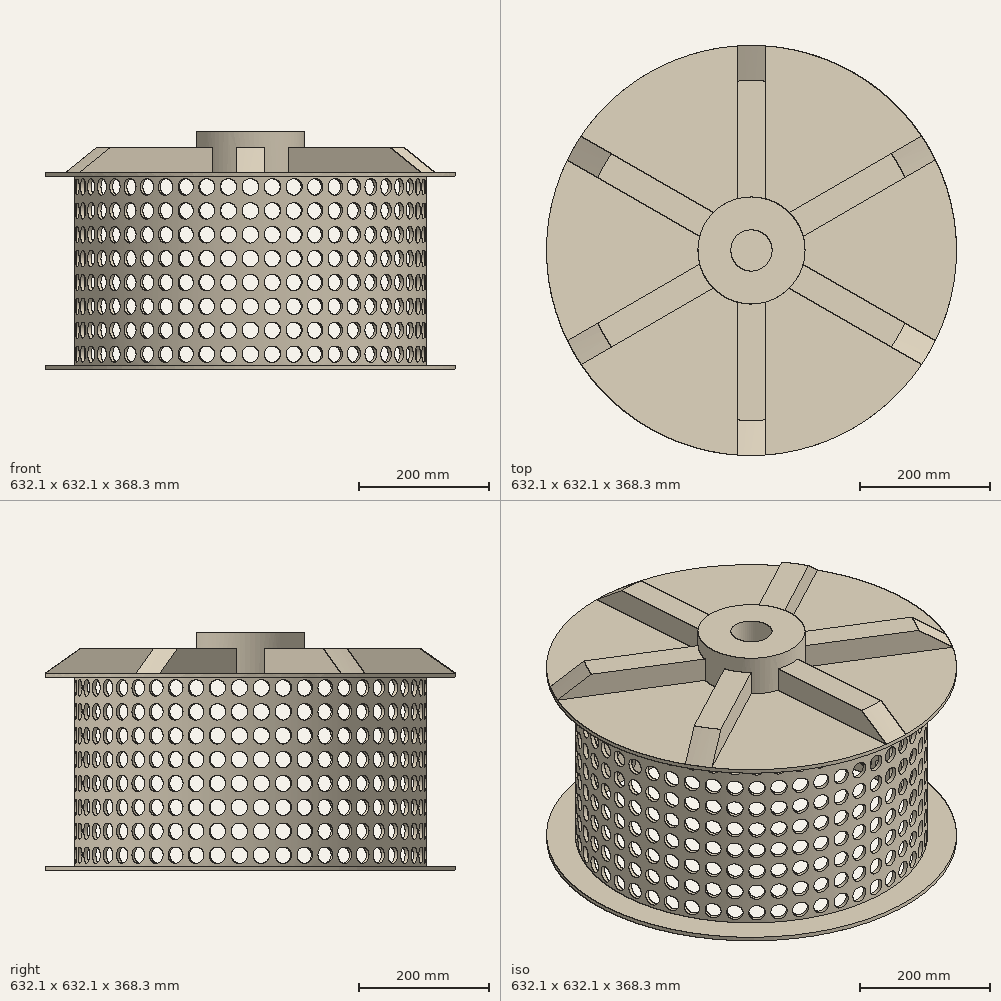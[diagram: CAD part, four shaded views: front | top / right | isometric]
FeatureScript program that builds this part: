
annotation { "Feature Type Name" : "Feature", "Feature Type Description" : "" }
export const myFeature = defineFeature(function(context is Context, id is Id, definition is map)
    precondition{}
    {
        {
            var Q0;
            Q0=qCreatedBy(makeId("Front.planeOp"),FACE);
            var sketch = newSketch(context, id + "F0", { "sketchPlane" : qUnion([Q0])});
            skLineSegment(sketch, "E0", {"start": v(265.27, 0) * mm, "end": v(316.07, 0) * mm});
            skLineSegment(sketch, "E1", {"start": v(316.07, 0) * mm, "end": v(316.07, 6.35) * mm});
            skLineSegment(sketch, "E2", {"start": v(316.07, 6.35) * mm, "end": v(265.27, 6.35) * mm});
            skLineSegment(sketch, "E3", {"start": v(265.27, 6.35) * mm, "end": v(265.27, 0) * mm});
            skLineSegment(sketch, "E4", {"start": v(265.27, 6.35) * mm, "end": v(265.27, 298.45) * mm});
            skLineSegment(sketch, "E5", {"start": v(265.27, 298.45) * mm, "end": v(271.62, 298.45) * mm});
            skLineSegment(sketch, "E6", {"start": v(271.62, 298.45) * mm, "end": v(271.62, 6.35) * mm});
            skLineSegment(sketch, "E7", {"start": v(265.27, 298.45) * mm, "end": v(265.27, 304.8) * mm});
            skLineSegment(sketch, "E8", {"start": v(265.27, 304.8) * mm, "end": v(316.07, 304.8) * mm});
            skLineSegment(sketch, "E9", {"start": v(316.07, 304.8) * mm, "end": v(316.07, 298.45) * mm});
            skLineSegment(sketch, "E10", {"start": v(316.07, 298.45) * mm, "end": v(271.62, 298.45) * mm});
            skLineSegment(sketch, "E11", {"start": v(0, -69.14) * mm, "end": v(0, 356.1) * mm, "construction": true});
            skLineSegment(sketch, "E12", {"start": v(265.27, 304.8) * mm, "end": v(0, 304.8) * mm});
            skLineSegment(sketch, "E13", {"start": v(0, 304.8) * mm, "end": v(0, 298.45) * mm});
            skLineSegment(sketch, "E14", {"start": v(0, 298.45) * mm, "end": v(265.27, 298.45) * mm});
            skSolve(sketch);
        }
        {
            var Q0;
            Q0=qSketchRegion(id+"F0",true);
            var Q1;
            Q1=sQuery(id+"F0.wireOp",EDGE,"E11");
            revolve(context, id + "F1", {"entities" : qUnion([Q0]), "axis" : qUnion([Q1]), "revolveType" : RevolveType.FULL});
        }
        {
            var Q0;
            Q0=makeQuery(id+"F1.opRevolve","SWEPT_FACE",FACE,{"disambiguationData":[OSD([sQuery(id+"F0.wireOp",EDGE,"E8"),sQuery(id+"F0.wireOp",EDGE,"E12")])]});
            var sketch = newSketch(context, id + "F2", { "sketchPlane" : qUnion([Q0])});
            skCircle(sketch, "E15", {"center": v(0, 0) * mm, "radius": 31.75 * mm});
            skCircle(sketch, "E16", {"center": v(0, 0) * mm, "radius": 82.55 * mm});
            skLineSegment(sketch, "E17.bottom", {"start": v(21.06, 315.86) * mm, "end": v(-21.41, 315.96) * mm});
            skLineSegment(sketch, "E17.left", {"start": v(21.06, 315.86) * mm, "end": v(21.41, 79.72) * mm});
            skLineSegment(sketch, "E17.right", {"start": v(-21.41, 315.96) * mm, "end": v(-21.06, 79.82) * mm});
            skPoint(sketch, "E17.middle", {"position": v(0, 197.84) * mm});
            skPoint(sketch, "E18.center", {"position": v(-0.43, 1.69) * mm});
            skLineSegment(sketch, "E19.1.0", {"start": v(-263.02, 176.17) * mm, "end": v(-284.33, 139.44) * mm});
            skLineSegment(sketch, "E19.1.1", {"start": v(-263.02, 176.17) * mm, "end": v(-58.34, 58.4) * mm});
            skLineSegment(sketch, "E19.1.2", {"start": v(-284.33, 139.44) * mm, "end": v(-79.65, 21.67) * mm});
            skLineSegment(sketch, "E19.2.0", {"start": v(-284.08, -139.7) * mm, "end": v(-262.92, -176.52) * mm});
            skLineSegment(sketch, "E19.2.1", {"start": v(-284.08, -139.7) * mm, "end": v(-79.75, -21.32) * mm});
            skLineSegment(sketch, "E19.2.2", {"start": v(-262.92, -176.52) * mm, "end": v(-58.6, -58.15) * mm});
            skLineSegment(sketch, "E19.3.0", {"start": v(-21.06, -315.86) * mm, "end": v(21.41, -315.96) * mm});
            skLineSegment(sketch, "E19.3.1", {"start": v(-21.06, -315.86) * mm, "end": v(-21.41, -79.72) * mm});
            skLineSegment(sketch, "E19.3.2", {"start": v(21.41, -315.96) * mm, "end": v(21.06, -79.82) * mm});
            skLineSegment(sketch, "E19.4.0", {"start": v(263.02, -176.17) * mm, "end": v(284.33, -139.44) * mm});
            skLineSegment(sketch, "E19.4.1", {"start": v(263.02, -176.17) * mm, "end": v(58.34, -58.4) * mm});
            skLineSegment(sketch, "E19.4.2", {"start": v(284.33, -139.44) * mm, "end": v(79.65, -21.67) * mm});
            skLineSegment(sketch, "E19.5.0", {"start": v(284.08, 139.7) * mm, "end": v(262.92, 176.52) * mm});
            skLineSegment(sketch, "E19.5.1", {"start": v(284.08, 139.7) * mm, "end": v(79.75, 21.32) * mm});
            skLineSegment(sketch, "E19.5.2", {"start": v(262.92, 176.52) * mm, "end": v(58.6, 58.15) * mm});
            skSolve(sketch);
        }
        {
            var Q0;
            Q0=makeQuery(id+"F2.imprint","IMPRINT",FACE,{"disambiguationData":[TD([[makeQuery(id+"F2.imprint","IMPRINT",EDGE,{"derivedFrom":sQuery(id+"F2.wireOp",EDGE,"E15")}),-1.0]])]});
            extrude(context, id + "F3", {"entities" : qUnion([Q0]), "operationType" : NewBodyOperationType.ADD, "depth" : 63.5 * mm, "offsetDistance" : 25.4 * mm});
        }
        {
            var Q0;
            {var subQ0=sQuery(id+"F2.wireOp",EDGE,"E19.1.1");var subQ1=sQuery(id+"F2.wireOp",EDGE,"E16");var subQ2=makeQuery(id+"F2.imprint","INTERSECT",VERTEX,{"derivedFrom":[subQ1,subQ0]});Q0=makeQuery(id+"F2.imprint","IMPRINT",FACE,{"disambiguationData":[TD([[makeQuery(id+"F2.imprint","IMPRINT",EDGE,{"disambiguationData":[TD([[subQ2,-1.0]])],"derivedFrom":subQ1}),-1.0]])]});}
            var Q1;
            {var subQ0=sQuery(id+"F2.wireOp",EDGE,"E17.left");var subQ1=sQuery(id+"F2.wireOp",EDGE,"E16");var subQ2=makeQuery(id+"F2.imprint","INTERSECT",VERTEX,{"derivedFrom":[subQ1,subQ0]});Q1=makeQuery(id+"F2.imprint","IMPRINT",FACE,{"disambiguationData":[TD([[makeQuery(id+"F2.imprint","IMPRINT",EDGE,{"disambiguationData":[TD([[subQ2,-1.0]])],"derivedFrom":subQ1}),-1.0]])]});}
            var Q2;
            {var subQ0=sQuery(id+"F2.wireOp",EDGE,"E19.5.1");var subQ1=sQuery(id+"F2.wireOp",EDGE,"E16");var subQ2=makeQuery(id+"F2.imprint","INTERSECT",VERTEX,{"derivedFrom":[subQ1,subQ0]});Q2=makeQuery(id+"F2.imprint","IMPRINT",FACE,{"disambiguationData":[TD([[makeQuery(id+"F2.imprint","IMPRINT",EDGE,{"disambiguationData":[TD([[subQ2,-1.0]])],"derivedFrom":subQ1}),-1.0]])]});}
            var Q3;
            {var subQ0=sQuery(id+"F2.wireOp",EDGE,"E19.4.1");var subQ1=sQuery(id+"F2.wireOp",EDGE,"E16");var subQ2=makeQuery(id+"F2.imprint","INTERSECT",VERTEX,{"derivedFrom":[subQ1,subQ0]});Q3=makeQuery(id+"F2.imprint","IMPRINT",FACE,{"disambiguationData":[TD([[makeQuery(id+"F2.imprint","IMPRINT",EDGE,{"disambiguationData":[TD([[subQ2,-1.0]])],"derivedFrom":subQ1}),-1.0]])]});}
            var Q4;
            {var subQ0=sQuery(id+"F2.wireOp",EDGE,"E19.3.1");var subQ1=sQuery(id+"F2.wireOp",EDGE,"E16");var subQ2=makeQuery(id+"F2.imprint","INTERSECT",VERTEX,{"derivedFrom":[subQ1,subQ0]});Q4=makeQuery(id+"F2.imprint","IMPRINT",FACE,{"disambiguationData":[TD([[makeQuery(id+"F2.imprint","IMPRINT",EDGE,{"disambiguationData":[TD([[subQ2,-1.0]])],"derivedFrom":subQ1}),-1.0]])]});}
            var Q5;
            {var subQ0=sQuery(id+"F2.wireOp",EDGE,"E19.2.1");var subQ1=sQuery(id+"F2.wireOp",EDGE,"E16");var subQ2=makeQuery(id+"F2.imprint","INTERSECT",VERTEX,{"derivedFrom":[subQ1,subQ0]});Q5=makeQuery(id+"F2.imprint","IMPRINT",FACE,{"disambiguationData":[TD([[makeQuery(id+"F2.imprint","IMPRINT",EDGE,{"disambiguationData":[TD([[subQ2,-1.0]])],"derivedFrom":subQ1}),-1.0]])]});}
            extrude(context, id + "F4", {"entities" : qUnion([Q0, Q1, Q2, Q3, Q4, Q5]), "operationType" : NewBodyOperationType.ADD, "depth" : 38.1 * mm, "offsetDistance" : 25.4 * mm});
        }
        {
            var Q0;
            Q0=qCreatedBy(makeId("Front.planeOp"),FACE);
            var sketch = newSketch(context, id + "F5", { "sketchPlane" : qUnion([Q0])});
            skPoint(sketch, "E20.0", {"position": v(316.07, 304.8) * mm});
            skLineSegment(sketch, "E21", {"start": v(316.07, 304.8) * mm, "end": v(257.94, 345.81) * mm});
            skLineSegment(sketch, "E22", {"start": v(257.94, 345.81) * mm, "end": v(316.07, 345.81) * mm});
            skLineSegment(sketch, "E23", {"start": v(316.07, 345.81) * mm, "end": v(316.07, 304.8) * mm});
            skSolve(sketch);
        }
        {
            var Q0;
            Q0=makeQuery(id+"F5.imprint","IMPRINT",FACE,{"disambiguationData":[TD([[makeQuery(id+"F5.imprint","IMPRINT",EDGE,{"derivedFrom":sQuery(id+"F5.wireOp",EDGE,"E21")}),-1.0]])]});
            var Q1;
            Q1=makeQuery(id+"F3.opExtrude","CAP_EDGE",EDGE,{"disambiguationData":[OSD([sQuery(id+"F2.wireOp",EDGE,"E16")])],"isStart":false});
            revolve(context, id + "F6", {"operationType" : NewBodyOperationType.REMOVE, "entities" : qUnion([Q0]), "axis" : qUnion([Q1]), "revolveType" : RevolveType.FULL, "oppositeDirection" : true});
        }
        {
            var Q0;
            Q0=qCreatedBy(makeId("Front.planeOp"),FACE);
            cPlane(context, id + "F7", {"entities" : qUnion([Q0]), "cplaneType" : CPlaneType.OFFSET, "offset" : 326.14 * mm, "width" : 152.4 * mm, "height" : 152.4 * mm});
        }
        {
            var Q0;
            Q0=qCreatedBy(id+"F7.planeOp",FACE);
            var sketch = newSketch(context, id + "F8", { "sketchPlane" : qUnion([Q0])});
            skCircle(sketch, "E24", {"center": v(0, 24.22) * mm, "radius": 12.7 * mm});
            skCircle(sketch, "E25.0.1.0", {"center": v(0, 61.05) * mm, "radius": 12.7 * mm});
            skCircle(sketch, "E25.0.2.0", {"center": v(0, 97.88) * mm, "radius": 12.7 * mm});
            skCircle(sketch, "E25.0.3.0", {"center": v(0, 134.7) * mm, "radius": 12.7 * mm});
            skCircle(sketch, "E25.0.4.0", {"center": v(0, 171.54) * mm, "radius": 12.7 * mm});
            skCircle(sketch, "E25.0.5.0", {"center": v(0, 208.37) * mm, "radius": 12.7 * mm});
            skCircle(sketch, "E25.0.6.0", {"center": v(0, 245.2) * mm, "radius": 12.7 * mm});
            skCircle(sketch, "E25.0.7.0", {"center": v(0, 282.03) * mm, "radius": 12.7 * mm});
            skLineSegment(sketch, "E25.direction1", {"start": v(0, 24.22) * mm, "end": v(25.4, 24.22) * mm, "construction": true});
            skLineSegment(sketch, "E25.direction2", {"start": v(0, 24.22) * mm, "end": v(0, 61.05) * mm, "construction": true});
            skSolve(sketch);
        }
        {
            var Q0;
            Q0=qSketchRegion(id+"F8",true);
            extrude(context, id + "F9", {"entities" : qUnion([Q0]), "oppositeDirection" : true, "depth" : 161.54 * mm, "offsetDistance" : 25.4 * mm});
        }
        {
            var Q0;
            Q0=makeQuery(id+"F9.opExtrude","SWEPT_BODY",BODY,{"disambiguationData":[OSD([sQuery(id+"F8.wireOp",EDGE,"E25.0.7.0")])]});
            var Q1;
            Q1=makeQuery(id+"F9.opExtrude","SWEPT_BODY",BODY,{"disambiguationData":[OSD([sQuery(id+"F8.wireOp",EDGE,"E25.0.6.0")])]});
            var Q2;
            Q2=makeQuery(id+"F9.opExtrude","SWEPT_BODY",BODY,{"disambiguationData":[OSD([sQuery(id+"F8.wireOp",EDGE,"E25.0.5.0")])]});
            var Q3;
            Q3=makeQuery(id+"F9.opExtrude","SWEPT_BODY",BODY,{"disambiguationData":[OSD([sQuery(id+"F8.wireOp",EDGE,"E25.0.4.0")])]});
            var Q4;
            Q4=makeQuery(id+"F9.opExtrude","SWEPT_BODY",BODY,{"disambiguationData":[OSD([sQuery(id+"F8.wireOp",EDGE,"E25.0.3.0")])]});
            var Q5;
            Q5=makeQuery(id+"F9.opExtrude","SWEPT_BODY",BODY,{"disambiguationData":[OSD([sQuery(id+"F8.wireOp",EDGE,"E25.0.2.0")])]});
            var Q6;
            Q6=makeQuery(id+"F9.opExtrude","SWEPT_BODY",BODY,{"disambiguationData":[OSD([sQuery(id+"F8.wireOp",EDGE,"E25.0.1.0")])]});
            var Q7;
            Q7=makeQuery(id+"F9.opExtrude","SWEPT_BODY",BODY,{"disambiguationData":[OSD([sQuery(id+"F8.wireOp",EDGE,"E24")])]});
            var Q8;
            Q8=makeQuery(id+"F3.opExtrude","CAP_EDGE",EDGE,{"disambiguationData":[OSD([sQuery(id+"F2.wireOp",EDGE,"E16")])],"isStart":false});
            circularPattern(context, id + "F10", {"entities" : qUnion([Q0, Q1, Q2, Q3, Q4, Q5, Q6, Q7]), "axis" : qUnion([Q8]), "angle" : 360 * degree, "instanceCount" : 50, "equalSpace" : true});
        }
        {
            var Q0;
            Q0=makeQuery(id+"F9.opExtrude","SWEPT_BODY",BODY,{"disambiguationData":[OSD([sQuery(id+"F8.wireOp",EDGE,"E24")])]});
            var Q1;
            Q1=makeQuery(id+"F9.opExtrude","SWEPT_BODY",BODY,{"disambiguationData":[OSD([sQuery(id+"F8.wireOp",EDGE,"E25.0.1.0")])]});
            var Q2;
            Q2=makeQuery(id+"F9.opExtrude","SWEPT_BODY",BODY,{"disambiguationData":[OSD([sQuery(id+"F8.wireOp",EDGE,"E25.0.2.0")])]});
            var Q3;
            Q3=makeQuery(id+"F9.opExtrude","SWEPT_BODY",BODY,{"disambiguationData":[OSD([sQuery(id+"F8.wireOp",EDGE,"E25.0.3.0")])]});
            var Q4;
            Q4=makeQuery(id+"F9.opExtrude","SWEPT_BODY",BODY,{"disambiguationData":[OSD([sQuery(id+"F8.wireOp",EDGE,"E25.0.4.0")])]});
            var Q5;
            Q5=makeQuery(id+"F9.opExtrude","SWEPT_BODY",BODY,{"disambiguationData":[OSD([sQuery(id+"F8.wireOp",EDGE,"E25.0.5.0")])]});
            var Q6;
            Q6=makeQuery(id+"F9.opExtrude","SWEPT_BODY",BODY,{"disambiguationData":[OSD([sQuery(id+"F8.wireOp",EDGE,"E25.0.6.0")])]});
            var Q7;
            Q7=makeQuery(id+"F9.opExtrude","SWEPT_BODY",BODY,{"disambiguationData":[OSD([sQuery(id+"F8.wireOp",EDGE,"E25.0.7.0")])]});
            var Q8;
            Q8=makeQuery(id+"F10.opPattern","COPY",BODY,{"derivedFrom":makeQuery(id+"F9.opExtrude","SWEPT_BODY",BODY,{"disambiguationData":[OSD([sQuery(id+"F8.wireOp",EDGE,"E24")])]}),"instanceName":"1"});
            var Q9;
            Q9=makeQuery(id+"F10.opPattern","COPY",BODY,{"derivedFrom":makeQuery(id+"F9.opExtrude","SWEPT_BODY",BODY,{"disambiguationData":[OSD([sQuery(id+"F8.wireOp",EDGE,"E25.0.1.0")])]}),"instanceName":"1"});
            var Q10;
            Q10=makeQuery(id+"F10.opPattern","COPY",BODY,{"derivedFrom":makeQuery(id+"F9.opExtrude","SWEPT_BODY",BODY,{"disambiguationData":[OSD([sQuery(id+"F8.wireOp",EDGE,"E25.0.2.0")])]}),"instanceName":"1"});
            var Q11;
            Q11=makeQuery(id+"F10.opPattern","COPY",BODY,{"derivedFrom":makeQuery(id+"F9.opExtrude","SWEPT_BODY",BODY,{"disambiguationData":[OSD([sQuery(id+"F8.wireOp",EDGE,"E25.0.3.0")])]}),"instanceName":"1"});
            var Q12;
            Q12=makeQuery(id+"F10.opPattern","COPY",BODY,{"derivedFrom":makeQuery(id+"F9.opExtrude","SWEPT_BODY",BODY,{"disambiguationData":[OSD([sQuery(id+"F8.wireOp",EDGE,"E25.0.4.0")])]}),"instanceName":"1"});
            var Q13;
            Q13=makeQuery(id+"F10.opPattern","COPY",BODY,{"derivedFrom":makeQuery(id+"F9.opExtrude","SWEPT_BODY",BODY,{"disambiguationData":[OSD([sQuery(id+"F8.wireOp",EDGE,"E25.0.5.0")])]}),"instanceName":"1"});
            var Q14;
            Q14=makeQuery(id+"F10.opPattern","COPY",BODY,{"derivedFrom":makeQuery(id+"F9.opExtrude","SWEPT_BODY",BODY,{"disambiguationData":[OSD([sQuery(id+"F8.wireOp",EDGE,"E25.0.6.0")])]}),"instanceName":"1"});
            var Q15;
            Q15=makeQuery(id+"F10.opPattern","COPY",BODY,{"derivedFrom":makeQuery(id+"F9.opExtrude","SWEPT_BODY",BODY,{"disambiguationData":[OSD([sQuery(id+"F8.wireOp",EDGE,"E25.0.7.0")])]}),"instanceName":"1"});
            var Q16;
            Q16=makeQuery(id+"F10.opPattern","COPY",BODY,{"derivedFrom":makeQuery(id+"F9.opExtrude","SWEPT_BODY",BODY,{"disambiguationData":[OSD([sQuery(id+"F8.wireOp",EDGE,"E24")])]}),"instanceName":"2"});
            var Q17;
            Q17=makeQuery(id+"F10.opPattern","COPY",BODY,{"derivedFrom":makeQuery(id+"F9.opExtrude","SWEPT_BODY",BODY,{"disambiguationData":[OSD([sQuery(id+"F8.wireOp",EDGE,"E25.0.1.0")])]}),"instanceName":"2"});
            var Q18;
            Q18=makeQuery(id+"F10.opPattern","COPY",BODY,{"derivedFrom":makeQuery(id+"F9.opExtrude","SWEPT_BODY",BODY,{"disambiguationData":[OSD([sQuery(id+"F8.wireOp",EDGE,"E25.0.2.0")])]}),"instanceName":"2"});
            var Q19;
            Q19=makeQuery(id+"F10.opPattern","COPY",BODY,{"derivedFrom":makeQuery(id+"F9.opExtrude","SWEPT_BODY",BODY,{"disambiguationData":[OSD([sQuery(id+"F8.wireOp",EDGE,"E25.0.3.0")])]}),"instanceName":"2"});
            var Q20;
            Q20=makeQuery(id+"F10.opPattern","COPY",BODY,{"derivedFrom":makeQuery(id+"F9.opExtrude","SWEPT_BODY",BODY,{"disambiguationData":[OSD([sQuery(id+"F8.wireOp",EDGE,"E25.0.4.0")])]}),"instanceName":"2"});
            var Q21;
            Q21=makeQuery(id+"F10.opPattern","COPY",BODY,{"derivedFrom":makeQuery(id+"F9.opExtrude","SWEPT_BODY",BODY,{"disambiguationData":[OSD([sQuery(id+"F8.wireOp",EDGE,"E25.0.5.0")])]}),"instanceName":"2"});
            var Q22;
            Q22=makeQuery(id+"F10.opPattern","COPY",BODY,{"derivedFrom":makeQuery(id+"F9.opExtrude","SWEPT_BODY",BODY,{"disambiguationData":[OSD([sQuery(id+"F8.wireOp",EDGE,"E25.0.6.0")])]}),"instanceName":"2"});
            var Q23;
            Q23=makeQuery(id+"F10.opPattern","COPY",BODY,{"derivedFrom":makeQuery(id+"F9.opExtrude","SWEPT_BODY",BODY,{"disambiguationData":[OSD([sQuery(id+"F8.wireOp",EDGE,"E25.0.7.0")])]}),"instanceName":"2"});
            var Q24;
            Q24=makeQuery(id+"F10.opPattern","COPY",BODY,{"derivedFrom":makeQuery(id+"F9.opExtrude","SWEPT_BODY",BODY,{"disambiguationData":[OSD([sQuery(id+"F8.wireOp",EDGE,"E24")])]}),"instanceName":"3"});
            var Q25;
            Q25=makeQuery(id+"F10.opPattern","COPY",BODY,{"derivedFrom":makeQuery(id+"F9.opExtrude","SWEPT_BODY",BODY,{"disambiguationData":[OSD([sQuery(id+"F8.wireOp",EDGE,"E25.0.1.0")])]}),"instanceName":"3"});
            var Q26;
            Q26=makeQuery(id+"F10.opPattern","COPY",BODY,{"derivedFrom":makeQuery(id+"F9.opExtrude","SWEPT_BODY",BODY,{"disambiguationData":[OSD([sQuery(id+"F8.wireOp",EDGE,"E25.0.2.0")])]}),"instanceName":"3"});
            var Q27;
            Q27=makeQuery(id+"F10.opPattern","COPY",BODY,{"derivedFrom":makeQuery(id+"F9.opExtrude","SWEPT_BODY",BODY,{"disambiguationData":[OSD([sQuery(id+"F8.wireOp",EDGE,"E25.0.3.0")])]}),"instanceName":"3"});
            var Q28;
            Q28=makeQuery(id+"F10.opPattern","COPY",BODY,{"derivedFrom":makeQuery(id+"F9.opExtrude","SWEPT_BODY",BODY,{"disambiguationData":[OSD([sQuery(id+"F8.wireOp",EDGE,"E25.0.4.0")])]}),"instanceName":"3"});
            var Q29;
            Q29=makeQuery(id+"F10.opPattern","COPY",BODY,{"derivedFrom":makeQuery(id+"F9.opExtrude","SWEPT_BODY",BODY,{"disambiguationData":[OSD([sQuery(id+"F8.wireOp",EDGE,"E25.0.5.0")])]}),"instanceName":"3"});
            var Q30;
            Q30=makeQuery(id+"F10.opPattern","COPY",BODY,{"derivedFrom":makeQuery(id+"F9.opExtrude","SWEPT_BODY",BODY,{"disambiguationData":[OSD([sQuery(id+"F8.wireOp",EDGE,"E25.0.6.0")])]}),"instanceName":"3"});
            var Q31;
            Q31=makeQuery(id+"F10.opPattern","COPY",BODY,{"derivedFrom":makeQuery(id+"F9.opExtrude","SWEPT_BODY",BODY,{"disambiguationData":[OSD([sQuery(id+"F8.wireOp",EDGE,"E25.0.7.0")])]}),"instanceName":"3"});
            var Q32;
            Q32=makeQuery(id+"F10.opPattern","COPY",BODY,{"derivedFrom":makeQuery(id+"F9.opExtrude","SWEPT_BODY",BODY,{"disambiguationData":[OSD([sQuery(id+"F8.wireOp",EDGE,"E24")])]}),"instanceName":"4"});
            var Q33;
            Q33=makeQuery(id+"F10.opPattern","COPY",BODY,{"derivedFrom":makeQuery(id+"F9.opExtrude","SWEPT_BODY",BODY,{"disambiguationData":[OSD([sQuery(id+"F8.wireOp",EDGE,"E25.0.1.0")])]}),"instanceName":"4"});
            var Q34;
            Q34=makeQuery(id+"F10.opPattern","COPY",BODY,{"derivedFrom":makeQuery(id+"F9.opExtrude","SWEPT_BODY",BODY,{"disambiguationData":[OSD([sQuery(id+"F8.wireOp",EDGE,"E25.0.2.0")])]}),"instanceName":"4"});
            var Q35;
            Q35=makeQuery(id+"F10.opPattern","COPY",BODY,{"derivedFrom":makeQuery(id+"F9.opExtrude","SWEPT_BODY",BODY,{"disambiguationData":[OSD([sQuery(id+"F8.wireOp",EDGE,"E25.0.3.0")])]}),"instanceName":"4"});
            var Q36;
            Q36=makeQuery(id+"F10.opPattern","COPY",BODY,{"derivedFrom":makeQuery(id+"F9.opExtrude","SWEPT_BODY",BODY,{"disambiguationData":[OSD([sQuery(id+"F8.wireOp",EDGE,"E25.0.4.0")])]}),"instanceName":"4"});
            var Q37;
            Q37=makeQuery(id+"F10.opPattern","COPY",BODY,{"derivedFrom":makeQuery(id+"F9.opExtrude","SWEPT_BODY",BODY,{"disambiguationData":[OSD([sQuery(id+"F8.wireOp",EDGE,"E25.0.5.0")])]}),"instanceName":"4"});
            var Q38;
            Q38=makeQuery(id+"F10.opPattern","COPY",BODY,{"derivedFrom":makeQuery(id+"F9.opExtrude","SWEPT_BODY",BODY,{"disambiguationData":[OSD([sQuery(id+"F8.wireOp",EDGE,"E25.0.6.0")])]}),"instanceName":"4"});
            var Q39;
            Q39=makeQuery(id+"F10.opPattern","COPY",BODY,{"derivedFrom":makeQuery(id+"F9.opExtrude","SWEPT_BODY",BODY,{"disambiguationData":[OSD([sQuery(id+"F8.wireOp",EDGE,"E25.0.7.0")])]}),"instanceName":"4"});
            var Q40;
            Q40=makeQuery(id+"F10.opPattern","COPY",BODY,{"derivedFrom":makeQuery(id+"F9.opExtrude","SWEPT_BODY",BODY,{"disambiguationData":[OSD([sQuery(id+"F8.wireOp",EDGE,"E24")])]}),"instanceName":"5"});
            var Q41;
            Q41=makeQuery(id+"F10.opPattern","COPY",BODY,{"derivedFrom":makeQuery(id+"F9.opExtrude","SWEPT_BODY",BODY,{"disambiguationData":[OSD([sQuery(id+"F8.wireOp",EDGE,"E25.0.1.0")])]}),"instanceName":"5"});
            var Q42;
            Q42=makeQuery(id+"F10.opPattern","COPY",BODY,{"derivedFrom":makeQuery(id+"F9.opExtrude","SWEPT_BODY",BODY,{"disambiguationData":[OSD([sQuery(id+"F8.wireOp",EDGE,"E25.0.2.0")])]}),"instanceName":"5"});
            var Q43;
            Q43=makeQuery(id+"F10.opPattern","COPY",BODY,{"derivedFrom":makeQuery(id+"F9.opExtrude","SWEPT_BODY",BODY,{"disambiguationData":[OSD([sQuery(id+"F8.wireOp",EDGE,"E25.0.3.0")])]}),"instanceName":"5"});
            var Q44;
            Q44=makeQuery(id+"F10.opPattern","COPY",BODY,{"derivedFrom":makeQuery(id+"F9.opExtrude","SWEPT_BODY",BODY,{"disambiguationData":[OSD([sQuery(id+"F8.wireOp",EDGE,"E25.0.4.0")])]}),"instanceName":"5"});
            var Q45;
            Q45=makeQuery(id+"F10.opPattern","COPY",BODY,{"derivedFrom":makeQuery(id+"F9.opExtrude","SWEPT_BODY",BODY,{"disambiguationData":[OSD([sQuery(id+"F8.wireOp",EDGE,"E25.0.5.0")])]}),"instanceName":"5"});
            var Q46;
            Q46=makeQuery(id+"F10.opPattern","COPY",BODY,{"derivedFrom":makeQuery(id+"F9.opExtrude","SWEPT_BODY",BODY,{"disambiguationData":[OSD([sQuery(id+"F8.wireOp",EDGE,"E25.0.6.0")])]}),"instanceName":"5"});
            var Q47;
            Q47=makeQuery(id+"F10.opPattern","COPY",BODY,{"derivedFrom":makeQuery(id+"F9.opExtrude","SWEPT_BODY",BODY,{"disambiguationData":[OSD([sQuery(id+"F8.wireOp",EDGE,"E25.0.7.0")])]}),"instanceName":"5"});
            var Q48;
            Q48=makeQuery(id+"F10.opPattern","COPY",BODY,{"derivedFrom":makeQuery(id+"F9.opExtrude","SWEPT_BODY",BODY,{"disambiguationData":[OSD([sQuery(id+"F8.wireOp",EDGE,"E24")])]}),"instanceName":"6"});
            var Q49;
            Q49=makeQuery(id+"F10.opPattern","COPY",BODY,{"derivedFrom":makeQuery(id+"F9.opExtrude","SWEPT_BODY",BODY,{"disambiguationData":[OSD([sQuery(id+"F8.wireOp",EDGE,"E25.0.1.0")])]}),"instanceName":"6"});
            var Q50;
            Q50=makeQuery(id+"F10.opPattern","COPY",BODY,{"derivedFrom":makeQuery(id+"F9.opExtrude","SWEPT_BODY",BODY,{"disambiguationData":[OSD([sQuery(id+"F8.wireOp",EDGE,"E25.0.2.0")])]}),"instanceName":"6"});
            var Q51;
            Q51=makeQuery(id+"F10.opPattern","COPY",BODY,{"derivedFrom":makeQuery(id+"F9.opExtrude","SWEPT_BODY",BODY,{"disambiguationData":[OSD([sQuery(id+"F8.wireOp",EDGE,"E25.0.3.0")])]}),"instanceName":"6"});
            var Q52;
            Q52=makeQuery(id+"F10.opPattern","COPY",BODY,{"derivedFrom":makeQuery(id+"F9.opExtrude","SWEPT_BODY",BODY,{"disambiguationData":[OSD([sQuery(id+"F8.wireOp",EDGE,"E25.0.4.0")])]}),"instanceName":"6"});
            var Q53;
            Q53=makeQuery(id+"F10.opPattern","COPY",BODY,{"derivedFrom":makeQuery(id+"F9.opExtrude","SWEPT_BODY",BODY,{"disambiguationData":[OSD([sQuery(id+"F8.wireOp",EDGE,"E25.0.5.0")])]}),"instanceName":"6"});
            var Q54;
            Q54=makeQuery(id+"F10.opPattern","COPY",BODY,{"derivedFrom":makeQuery(id+"F9.opExtrude","SWEPT_BODY",BODY,{"disambiguationData":[OSD([sQuery(id+"F8.wireOp",EDGE,"E25.0.6.0")])]}),"instanceName":"6"});
            var Q55;
            Q55=makeQuery(id+"F10.opPattern","COPY",BODY,{"derivedFrom":makeQuery(id+"F9.opExtrude","SWEPT_BODY",BODY,{"disambiguationData":[OSD([sQuery(id+"F8.wireOp",EDGE,"E25.0.7.0")])]}),"instanceName":"6"});
            var Q56;
            Q56=makeQuery(id+"F10.opPattern","COPY",BODY,{"derivedFrom":makeQuery(id+"F9.opExtrude","SWEPT_BODY",BODY,{"disambiguationData":[OSD([sQuery(id+"F8.wireOp",EDGE,"E24")])]}),"instanceName":"7"});
            var Q57;
            Q57=makeQuery(id+"F10.opPattern","COPY",BODY,{"derivedFrom":makeQuery(id+"F9.opExtrude","SWEPT_BODY",BODY,{"disambiguationData":[OSD([sQuery(id+"F8.wireOp",EDGE,"E25.0.1.0")])]}),"instanceName":"7"});
            var Q58;
            Q58=makeQuery(id+"F10.opPattern","COPY",BODY,{"derivedFrom":makeQuery(id+"F9.opExtrude","SWEPT_BODY",BODY,{"disambiguationData":[OSD([sQuery(id+"F8.wireOp",EDGE,"E25.0.2.0")])]}),"instanceName":"7"});
            var Q59;
            Q59=makeQuery(id+"F10.opPattern","COPY",BODY,{"derivedFrom":makeQuery(id+"F9.opExtrude","SWEPT_BODY",BODY,{"disambiguationData":[OSD([sQuery(id+"F8.wireOp",EDGE,"E25.0.3.0")])]}),"instanceName":"7"});
            var Q60;
            Q60=makeQuery(id+"F10.opPattern","COPY",BODY,{"derivedFrom":makeQuery(id+"F9.opExtrude","SWEPT_BODY",BODY,{"disambiguationData":[OSD([sQuery(id+"F8.wireOp",EDGE,"E25.0.4.0")])]}),"instanceName":"7"});
            var Q61;
            Q61=makeQuery(id+"F10.opPattern","COPY",BODY,{"derivedFrom":makeQuery(id+"F9.opExtrude","SWEPT_BODY",BODY,{"disambiguationData":[OSD([sQuery(id+"F8.wireOp",EDGE,"E25.0.5.0")])]}),"instanceName":"7"});
            var Q62;
            Q62=makeQuery(id+"F10.opPattern","COPY",BODY,{"derivedFrom":makeQuery(id+"F9.opExtrude","SWEPT_BODY",BODY,{"disambiguationData":[OSD([sQuery(id+"F8.wireOp",EDGE,"E25.0.6.0")])]}),"instanceName":"7"});
            var Q63;
            Q63=makeQuery(id+"F10.opPattern","COPY",BODY,{"derivedFrom":makeQuery(id+"F9.opExtrude","SWEPT_BODY",BODY,{"disambiguationData":[OSD([sQuery(id+"F8.wireOp",EDGE,"E25.0.7.0")])]}),"instanceName":"7"});
            var Q64;
            Q64=makeQuery(id+"F10.opPattern","COPY",BODY,{"derivedFrom":makeQuery(id+"F9.opExtrude","SWEPT_BODY",BODY,{"disambiguationData":[OSD([sQuery(id+"F8.wireOp",EDGE,"E24")])]}),"instanceName":"8"});
            var Q65;
            Q65=makeQuery(id+"F10.opPattern","COPY",BODY,{"derivedFrom":makeQuery(id+"F9.opExtrude","SWEPT_BODY",BODY,{"disambiguationData":[OSD([sQuery(id+"F8.wireOp",EDGE,"E25.0.1.0")])]}),"instanceName":"8"});
            var Q66;
            Q66=makeQuery(id+"F10.opPattern","COPY",BODY,{"derivedFrom":makeQuery(id+"F9.opExtrude","SWEPT_BODY",BODY,{"disambiguationData":[OSD([sQuery(id+"F8.wireOp",EDGE,"E25.0.2.0")])]}),"instanceName":"8"});
            var Q67;
            Q67=makeQuery(id+"F10.opPattern","COPY",BODY,{"derivedFrom":makeQuery(id+"F9.opExtrude","SWEPT_BODY",BODY,{"disambiguationData":[OSD([sQuery(id+"F8.wireOp",EDGE,"E25.0.3.0")])]}),"instanceName":"8"});
            var Q68;
            Q68=makeQuery(id+"F10.opPattern","COPY",BODY,{"derivedFrom":makeQuery(id+"F9.opExtrude","SWEPT_BODY",BODY,{"disambiguationData":[OSD([sQuery(id+"F8.wireOp",EDGE,"E25.0.4.0")])]}),"instanceName":"8"});
            var Q69;
            Q69=makeQuery(id+"F10.opPattern","COPY",BODY,{"derivedFrom":makeQuery(id+"F9.opExtrude","SWEPT_BODY",BODY,{"disambiguationData":[OSD([sQuery(id+"F8.wireOp",EDGE,"E25.0.5.0")])]}),"instanceName":"8"});
            var Q70;
            Q70=makeQuery(id+"F10.opPattern","COPY",BODY,{"derivedFrom":makeQuery(id+"F9.opExtrude","SWEPT_BODY",BODY,{"disambiguationData":[OSD([sQuery(id+"F8.wireOp",EDGE,"E25.0.6.0")])]}),"instanceName":"8"});
            var Q71;
            Q71=makeQuery(id+"F10.opPattern","COPY",BODY,{"derivedFrom":makeQuery(id+"F9.opExtrude","SWEPT_BODY",BODY,{"disambiguationData":[OSD([sQuery(id+"F8.wireOp",EDGE,"E25.0.7.0")])]}),"instanceName":"8"});
            var Q72;
            Q72=makeQuery(id+"F10.opPattern","COPY",BODY,{"derivedFrom":makeQuery(id+"F9.opExtrude","SWEPT_BODY",BODY,{"disambiguationData":[OSD([sQuery(id+"F8.wireOp",EDGE,"E24")])]}),"instanceName":"9"});
            var Q73;
            Q73=makeQuery(id+"F10.opPattern","COPY",BODY,{"derivedFrom":makeQuery(id+"F9.opExtrude","SWEPT_BODY",BODY,{"disambiguationData":[OSD([sQuery(id+"F8.wireOp",EDGE,"E25.0.1.0")])]}),"instanceName":"9"});
            var Q74;
            Q74=makeQuery(id+"F10.opPattern","COPY",BODY,{"derivedFrom":makeQuery(id+"F9.opExtrude","SWEPT_BODY",BODY,{"disambiguationData":[OSD([sQuery(id+"F8.wireOp",EDGE,"E25.0.2.0")])]}),"instanceName":"9"});
            var Q75;
            Q75=makeQuery(id+"F10.opPattern","COPY",BODY,{"derivedFrom":makeQuery(id+"F9.opExtrude","SWEPT_BODY",BODY,{"disambiguationData":[OSD([sQuery(id+"F8.wireOp",EDGE,"E25.0.3.0")])]}),"instanceName":"9"});
            var Q76;
            Q76=makeQuery(id+"F10.opPattern","COPY",BODY,{"derivedFrom":makeQuery(id+"F9.opExtrude","SWEPT_BODY",BODY,{"disambiguationData":[OSD([sQuery(id+"F8.wireOp",EDGE,"E25.0.4.0")])]}),"instanceName":"9"});
            var Q77;
            Q77=makeQuery(id+"F10.opPattern","COPY",BODY,{"derivedFrom":makeQuery(id+"F9.opExtrude","SWEPT_BODY",BODY,{"disambiguationData":[OSD([sQuery(id+"F8.wireOp",EDGE,"E25.0.5.0")])]}),"instanceName":"9"});
            var Q78;
            Q78=makeQuery(id+"F10.opPattern","COPY",BODY,{"derivedFrom":makeQuery(id+"F9.opExtrude","SWEPT_BODY",BODY,{"disambiguationData":[OSD([sQuery(id+"F8.wireOp",EDGE,"E25.0.6.0")])]}),"instanceName":"9"});
            var Q79;
            Q79=makeQuery(id+"F10.opPattern","COPY",BODY,{"derivedFrom":makeQuery(id+"F9.opExtrude","SWEPT_BODY",BODY,{"disambiguationData":[OSD([sQuery(id+"F8.wireOp",EDGE,"E25.0.7.0")])]}),"instanceName":"9"});
            var Q80;
            Q80=makeQuery(id+"F10.opPattern","COPY",BODY,{"derivedFrom":makeQuery(id+"F9.opExtrude","SWEPT_BODY",BODY,{"disambiguationData":[OSD([sQuery(id+"F8.wireOp",EDGE,"E24")])]}),"instanceName":"10"});
            var Q81;
            Q81=makeQuery(id+"F10.opPattern","COPY",BODY,{"derivedFrom":makeQuery(id+"F9.opExtrude","SWEPT_BODY",BODY,{"disambiguationData":[OSD([sQuery(id+"F8.wireOp",EDGE,"E25.0.1.0")])]}),"instanceName":"10"});
            var Q82;
            Q82=makeQuery(id+"F10.opPattern","COPY",BODY,{"derivedFrom":makeQuery(id+"F9.opExtrude","SWEPT_BODY",BODY,{"disambiguationData":[OSD([sQuery(id+"F8.wireOp",EDGE,"E25.0.2.0")])]}),"instanceName":"10"});
            var Q83;
            Q83=makeQuery(id+"F10.opPattern","COPY",BODY,{"derivedFrom":makeQuery(id+"F9.opExtrude","SWEPT_BODY",BODY,{"disambiguationData":[OSD([sQuery(id+"F8.wireOp",EDGE,"E25.0.3.0")])]}),"instanceName":"10"});
            var Q84;
            Q84=makeQuery(id+"F10.opPattern","COPY",BODY,{"derivedFrom":makeQuery(id+"F9.opExtrude","SWEPT_BODY",BODY,{"disambiguationData":[OSD([sQuery(id+"F8.wireOp",EDGE,"E25.0.4.0")])]}),"instanceName":"10"});
            var Q85;
            Q85=makeQuery(id+"F10.opPattern","COPY",BODY,{"derivedFrom":makeQuery(id+"F9.opExtrude","SWEPT_BODY",BODY,{"disambiguationData":[OSD([sQuery(id+"F8.wireOp",EDGE,"E25.0.5.0")])]}),"instanceName":"10"});
            var Q86;
            Q86=makeQuery(id+"F10.opPattern","COPY",BODY,{"derivedFrom":makeQuery(id+"F9.opExtrude","SWEPT_BODY",BODY,{"disambiguationData":[OSD([sQuery(id+"F8.wireOp",EDGE,"E25.0.6.0")])]}),"instanceName":"10"});
            var Q87;
            Q87=makeQuery(id+"F10.opPattern","COPY",BODY,{"derivedFrom":makeQuery(id+"F9.opExtrude","SWEPT_BODY",BODY,{"disambiguationData":[OSD([sQuery(id+"F8.wireOp",EDGE,"E25.0.7.0")])]}),"instanceName":"10"});
            var Q88;
            Q88=makeQuery(id+"F10.opPattern","COPY",BODY,{"derivedFrom":makeQuery(id+"F9.opExtrude","SWEPT_BODY",BODY,{"disambiguationData":[OSD([sQuery(id+"F8.wireOp",EDGE,"E24")])]}),"instanceName":"11"});
            var Q89;
            Q89=makeQuery(id+"F10.opPattern","COPY",BODY,{"derivedFrom":makeQuery(id+"F9.opExtrude","SWEPT_BODY",BODY,{"disambiguationData":[OSD([sQuery(id+"F8.wireOp",EDGE,"E25.0.1.0")])]}),"instanceName":"11"});
            var Q90;
            Q90=makeQuery(id+"F10.opPattern","COPY",BODY,{"derivedFrom":makeQuery(id+"F9.opExtrude","SWEPT_BODY",BODY,{"disambiguationData":[OSD([sQuery(id+"F8.wireOp",EDGE,"E25.0.2.0")])]}),"instanceName":"11"});
            var Q91;
            Q91=makeQuery(id+"F10.opPattern","COPY",BODY,{"derivedFrom":makeQuery(id+"F9.opExtrude","SWEPT_BODY",BODY,{"disambiguationData":[OSD([sQuery(id+"F8.wireOp",EDGE,"E25.0.3.0")])]}),"instanceName":"11"});
            var Q92;
            Q92=makeQuery(id+"F10.opPattern","COPY",BODY,{"derivedFrom":makeQuery(id+"F9.opExtrude","SWEPT_BODY",BODY,{"disambiguationData":[OSD([sQuery(id+"F8.wireOp",EDGE,"E25.0.4.0")])]}),"instanceName":"11"});
            var Q93;
            Q93=makeQuery(id+"F10.opPattern","COPY",BODY,{"derivedFrom":makeQuery(id+"F9.opExtrude","SWEPT_BODY",BODY,{"disambiguationData":[OSD([sQuery(id+"F8.wireOp",EDGE,"E25.0.5.0")])]}),"instanceName":"11"});
            var Q94;
            Q94=makeQuery(id+"F10.opPattern","COPY",BODY,{"derivedFrom":makeQuery(id+"F9.opExtrude","SWEPT_BODY",BODY,{"disambiguationData":[OSD([sQuery(id+"F8.wireOp",EDGE,"E25.0.6.0")])]}),"instanceName":"11"});
            var Q95;
            Q95=makeQuery(id+"F10.opPattern","COPY",BODY,{"derivedFrom":makeQuery(id+"F9.opExtrude","SWEPT_BODY",BODY,{"disambiguationData":[OSD([sQuery(id+"F8.wireOp",EDGE,"E25.0.7.0")])]}),"instanceName":"11"});
            var Q96;
            Q96=makeQuery(id+"F10.opPattern","COPY",BODY,{"derivedFrom":makeQuery(id+"F9.opExtrude","SWEPT_BODY",BODY,{"disambiguationData":[OSD([sQuery(id+"F8.wireOp",EDGE,"E24")])]}),"instanceName":"12"});
            var Q97;
            Q97=makeQuery(id+"F10.opPattern","COPY",BODY,{"derivedFrom":makeQuery(id+"F9.opExtrude","SWEPT_BODY",BODY,{"disambiguationData":[OSD([sQuery(id+"F8.wireOp",EDGE,"E25.0.1.0")])]}),"instanceName":"12"});
            var Q98;
            Q98=makeQuery(id+"F10.opPattern","COPY",BODY,{"derivedFrom":makeQuery(id+"F9.opExtrude","SWEPT_BODY",BODY,{"disambiguationData":[OSD([sQuery(id+"F8.wireOp",EDGE,"E25.0.2.0")])]}),"instanceName":"12"});
            var Q99;
            Q99=makeQuery(id+"F10.opPattern","COPY",BODY,{"derivedFrom":makeQuery(id+"F9.opExtrude","SWEPT_BODY",BODY,{"disambiguationData":[OSD([sQuery(id+"F8.wireOp",EDGE,"E25.0.3.0")])]}),"instanceName":"12"});
            var Q100;
            Q100=makeQuery(id+"F10.opPattern","COPY",BODY,{"derivedFrom":makeQuery(id+"F9.opExtrude","SWEPT_BODY",BODY,{"disambiguationData":[OSD([sQuery(id+"F8.wireOp",EDGE,"E25.0.4.0")])]}),"instanceName":"12"});
            var Q101;
            Q101=makeQuery(id+"F10.opPattern","COPY",BODY,{"derivedFrom":makeQuery(id+"F9.opExtrude","SWEPT_BODY",BODY,{"disambiguationData":[OSD([sQuery(id+"F8.wireOp",EDGE,"E25.0.5.0")])]}),"instanceName":"12"});
            var Q102;
            Q102=makeQuery(id+"F10.opPattern","COPY",BODY,{"derivedFrom":makeQuery(id+"F9.opExtrude","SWEPT_BODY",BODY,{"disambiguationData":[OSD([sQuery(id+"F8.wireOp",EDGE,"E25.0.6.0")])]}),"instanceName":"12"});
            var Q103;
            Q103=makeQuery(id+"F10.opPattern","COPY",BODY,{"derivedFrom":makeQuery(id+"F9.opExtrude","SWEPT_BODY",BODY,{"disambiguationData":[OSD([sQuery(id+"F8.wireOp",EDGE,"E25.0.7.0")])]}),"instanceName":"12"});
            var Q104;
            Q104=makeQuery(id+"F10.opPattern","COPY",BODY,{"derivedFrom":makeQuery(id+"F9.opExtrude","SWEPT_BODY",BODY,{"disambiguationData":[OSD([sQuery(id+"F8.wireOp",EDGE,"E24")])]}),"instanceName":"13"});
            var Q105;
            Q105=makeQuery(id+"F10.opPattern","COPY",BODY,{"derivedFrom":makeQuery(id+"F9.opExtrude","SWEPT_BODY",BODY,{"disambiguationData":[OSD([sQuery(id+"F8.wireOp",EDGE,"E25.0.1.0")])]}),"instanceName":"13"});
            var Q106;
            Q106=makeQuery(id+"F10.opPattern","COPY",BODY,{"derivedFrom":makeQuery(id+"F9.opExtrude","SWEPT_BODY",BODY,{"disambiguationData":[OSD([sQuery(id+"F8.wireOp",EDGE,"E25.0.2.0")])]}),"instanceName":"13"});
            var Q107;
            Q107=makeQuery(id+"F10.opPattern","COPY",BODY,{"derivedFrom":makeQuery(id+"F9.opExtrude","SWEPT_BODY",BODY,{"disambiguationData":[OSD([sQuery(id+"F8.wireOp",EDGE,"E25.0.3.0")])]}),"instanceName":"13"});
            var Q108;
            Q108=makeQuery(id+"F10.opPattern","COPY",BODY,{"derivedFrom":makeQuery(id+"F9.opExtrude","SWEPT_BODY",BODY,{"disambiguationData":[OSD([sQuery(id+"F8.wireOp",EDGE,"E25.0.4.0")])]}),"instanceName":"13"});
            var Q109;
            Q109=makeQuery(id+"F10.opPattern","COPY",BODY,{"derivedFrom":makeQuery(id+"F9.opExtrude","SWEPT_BODY",BODY,{"disambiguationData":[OSD([sQuery(id+"F8.wireOp",EDGE,"E25.0.5.0")])]}),"instanceName":"13"});
            var Q110;
            Q110=makeQuery(id+"F10.opPattern","COPY",BODY,{"derivedFrom":makeQuery(id+"F9.opExtrude","SWEPT_BODY",BODY,{"disambiguationData":[OSD([sQuery(id+"F8.wireOp",EDGE,"E25.0.6.0")])]}),"instanceName":"13"});
            var Q111;
            Q111=makeQuery(id+"F10.opPattern","COPY",BODY,{"derivedFrom":makeQuery(id+"F9.opExtrude","SWEPT_BODY",BODY,{"disambiguationData":[OSD([sQuery(id+"F8.wireOp",EDGE,"E25.0.7.0")])]}),"instanceName":"13"});
            var Q112;
            Q112=makeQuery(id+"F10.opPattern","COPY",BODY,{"derivedFrom":makeQuery(id+"F9.opExtrude","SWEPT_BODY",BODY,{"disambiguationData":[OSD([sQuery(id+"F8.wireOp",EDGE,"E24")])]}),"instanceName":"14"});
            var Q113;
            Q113=makeQuery(id+"F10.opPattern","COPY",BODY,{"derivedFrom":makeQuery(id+"F9.opExtrude","SWEPT_BODY",BODY,{"disambiguationData":[OSD([sQuery(id+"F8.wireOp",EDGE,"E25.0.1.0")])]}),"instanceName":"14"});
            var Q114;
            Q114=makeQuery(id+"F10.opPattern","COPY",BODY,{"derivedFrom":makeQuery(id+"F9.opExtrude","SWEPT_BODY",BODY,{"disambiguationData":[OSD([sQuery(id+"F8.wireOp",EDGE,"E25.0.2.0")])]}),"instanceName":"14"});
            var Q115;
            Q115=makeQuery(id+"F10.opPattern","COPY",BODY,{"derivedFrom":makeQuery(id+"F9.opExtrude","SWEPT_BODY",BODY,{"disambiguationData":[OSD([sQuery(id+"F8.wireOp",EDGE,"E25.0.3.0")])]}),"instanceName":"14"});
            var Q116;
            Q116=makeQuery(id+"F10.opPattern","COPY",BODY,{"derivedFrom":makeQuery(id+"F9.opExtrude","SWEPT_BODY",BODY,{"disambiguationData":[OSD([sQuery(id+"F8.wireOp",EDGE,"E25.0.4.0")])]}),"instanceName":"14"});
            var Q117;
            Q117=makeQuery(id+"F10.opPattern","COPY",BODY,{"derivedFrom":makeQuery(id+"F9.opExtrude","SWEPT_BODY",BODY,{"disambiguationData":[OSD([sQuery(id+"F8.wireOp",EDGE,"E25.0.5.0")])]}),"instanceName":"14"});
            var Q118;
            Q118=makeQuery(id+"F10.opPattern","COPY",BODY,{"derivedFrom":makeQuery(id+"F9.opExtrude","SWEPT_BODY",BODY,{"disambiguationData":[OSD([sQuery(id+"F8.wireOp",EDGE,"E25.0.6.0")])]}),"instanceName":"14"});
            var Q119;
            Q119=makeQuery(id+"F10.opPattern","COPY",BODY,{"derivedFrom":makeQuery(id+"F9.opExtrude","SWEPT_BODY",BODY,{"disambiguationData":[OSD([sQuery(id+"F8.wireOp",EDGE,"E25.0.7.0")])]}),"instanceName":"14"});
            var Q120;
            Q120=makeQuery(id+"F10.opPattern","COPY",BODY,{"derivedFrom":makeQuery(id+"F9.opExtrude","SWEPT_BODY",BODY,{"disambiguationData":[OSD([sQuery(id+"F8.wireOp",EDGE,"E24")])]}),"instanceName":"15"});
            var Q121;
            Q121=makeQuery(id+"F10.opPattern","COPY",BODY,{"derivedFrom":makeQuery(id+"F9.opExtrude","SWEPT_BODY",BODY,{"disambiguationData":[OSD([sQuery(id+"F8.wireOp",EDGE,"E25.0.1.0")])]}),"instanceName":"15"});
            var Q122;
            Q122=makeQuery(id+"F10.opPattern","COPY",BODY,{"derivedFrom":makeQuery(id+"F9.opExtrude","SWEPT_BODY",BODY,{"disambiguationData":[OSD([sQuery(id+"F8.wireOp",EDGE,"E25.0.2.0")])]}),"instanceName":"15"});
            var Q123;
            Q123=makeQuery(id+"F10.opPattern","COPY",BODY,{"derivedFrom":makeQuery(id+"F9.opExtrude","SWEPT_BODY",BODY,{"disambiguationData":[OSD([sQuery(id+"F8.wireOp",EDGE,"E25.0.3.0")])]}),"instanceName":"15"});
            var Q124;
            Q124=makeQuery(id+"F10.opPattern","COPY",BODY,{"derivedFrom":makeQuery(id+"F9.opExtrude","SWEPT_BODY",BODY,{"disambiguationData":[OSD([sQuery(id+"F8.wireOp",EDGE,"E25.0.4.0")])]}),"instanceName":"15"});
            var Q125;
            Q125=makeQuery(id+"F10.opPattern","COPY",BODY,{"derivedFrom":makeQuery(id+"F9.opExtrude","SWEPT_BODY",BODY,{"disambiguationData":[OSD([sQuery(id+"F8.wireOp",EDGE,"E25.0.5.0")])]}),"instanceName":"15"});
            var Q126;
            Q126=makeQuery(id+"F10.opPattern","COPY",BODY,{"derivedFrom":makeQuery(id+"F9.opExtrude","SWEPT_BODY",BODY,{"disambiguationData":[OSD([sQuery(id+"F8.wireOp",EDGE,"E25.0.6.0")])]}),"instanceName":"15"});
            var Q127;
            Q127=makeQuery(id+"F10.opPattern","COPY",BODY,{"derivedFrom":makeQuery(id+"F9.opExtrude","SWEPT_BODY",BODY,{"disambiguationData":[OSD([sQuery(id+"F8.wireOp",EDGE,"E25.0.7.0")])]}),"instanceName":"15"});
            var Q128;
            Q128=makeQuery(id+"F10.opPattern","COPY",BODY,{"derivedFrom":makeQuery(id+"F9.opExtrude","SWEPT_BODY",BODY,{"disambiguationData":[OSD([sQuery(id+"F8.wireOp",EDGE,"E24")])]}),"instanceName":"16"});
            var Q129;
            Q129=makeQuery(id+"F10.opPattern","COPY",BODY,{"derivedFrom":makeQuery(id+"F9.opExtrude","SWEPT_BODY",BODY,{"disambiguationData":[OSD([sQuery(id+"F8.wireOp",EDGE,"E25.0.1.0")])]}),"instanceName":"16"});
            var Q130;
            Q130=makeQuery(id+"F10.opPattern","COPY",BODY,{"derivedFrom":makeQuery(id+"F9.opExtrude","SWEPT_BODY",BODY,{"disambiguationData":[OSD([sQuery(id+"F8.wireOp",EDGE,"E25.0.2.0")])]}),"instanceName":"16"});
            var Q131;
            Q131=makeQuery(id+"F10.opPattern","COPY",BODY,{"derivedFrom":makeQuery(id+"F9.opExtrude","SWEPT_BODY",BODY,{"disambiguationData":[OSD([sQuery(id+"F8.wireOp",EDGE,"E25.0.3.0")])]}),"instanceName":"16"});
            var Q132;
            Q132=makeQuery(id+"F10.opPattern","COPY",BODY,{"derivedFrom":makeQuery(id+"F9.opExtrude","SWEPT_BODY",BODY,{"disambiguationData":[OSD([sQuery(id+"F8.wireOp",EDGE,"E25.0.4.0")])]}),"instanceName":"16"});
            var Q133;
            Q133=makeQuery(id+"F10.opPattern","COPY",BODY,{"derivedFrom":makeQuery(id+"F9.opExtrude","SWEPT_BODY",BODY,{"disambiguationData":[OSD([sQuery(id+"F8.wireOp",EDGE,"E25.0.5.0")])]}),"instanceName":"16"});
            var Q134;
            Q134=makeQuery(id+"F10.opPattern","COPY",BODY,{"derivedFrom":makeQuery(id+"F9.opExtrude","SWEPT_BODY",BODY,{"disambiguationData":[OSD([sQuery(id+"F8.wireOp",EDGE,"E25.0.6.0")])]}),"instanceName":"16"});
            var Q135;
            Q135=makeQuery(id+"F10.opPattern","COPY",BODY,{"derivedFrom":makeQuery(id+"F9.opExtrude","SWEPT_BODY",BODY,{"disambiguationData":[OSD([sQuery(id+"F8.wireOp",EDGE,"E25.0.7.0")])]}),"instanceName":"16"});
            var Q136;
            Q136=makeQuery(id+"F10.opPattern","COPY",BODY,{"derivedFrom":makeQuery(id+"F9.opExtrude","SWEPT_BODY",BODY,{"disambiguationData":[OSD([sQuery(id+"F8.wireOp",EDGE,"E24")])]}),"instanceName":"17"});
            var Q137;
            Q137=makeQuery(id+"F10.opPattern","COPY",BODY,{"derivedFrom":makeQuery(id+"F9.opExtrude","SWEPT_BODY",BODY,{"disambiguationData":[OSD([sQuery(id+"F8.wireOp",EDGE,"E25.0.1.0")])]}),"instanceName":"17"});
            var Q138;
            Q138=makeQuery(id+"F10.opPattern","COPY",BODY,{"derivedFrom":makeQuery(id+"F9.opExtrude","SWEPT_BODY",BODY,{"disambiguationData":[OSD([sQuery(id+"F8.wireOp",EDGE,"E25.0.2.0")])]}),"instanceName":"17"});
            var Q139;
            Q139=makeQuery(id+"F10.opPattern","COPY",BODY,{"derivedFrom":makeQuery(id+"F9.opExtrude","SWEPT_BODY",BODY,{"disambiguationData":[OSD([sQuery(id+"F8.wireOp",EDGE,"E25.0.3.0")])]}),"instanceName":"17"});
            var Q140;
            Q140=makeQuery(id+"F10.opPattern","COPY",BODY,{"derivedFrom":makeQuery(id+"F9.opExtrude","SWEPT_BODY",BODY,{"disambiguationData":[OSD([sQuery(id+"F8.wireOp",EDGE,"E25.0.4.0")])]}),"instanceName":"17"});
            var Q141;
            Q141=makeQuery(id+"F10.opPattern","COPY",BODY,{"derivedFrom":makeQuery(id+"F9.opExtrude","SWEPT_BODY",BODY,{"disambiguationData":[OSD([sQuery(id+"F8.wireOp",EDGE,"E25.0.5.0")])]}),"instanceName":"17"});
            var Q142;
            Q142=makeQuery(id+"F10.opPattern","COPY",BODY,{"derivedFrom":makeQuery(id+"F9.opExtrude","SWEPT_BODY",BODY,{"disambiguationData":[OSD([sQuery(id+"F8.wireOp",EDGE,"E25.0.6.0")])]}),"instanceName":"17"});
            var Q143;
            Q143=makeQuery(id+"F10.opPattern","COPY",BODY,{"derivedFrom":makeQuery(id+"F9.opExtrude","SWEPT_BODY",BODY,{"disambiguationData":[OSD([sQuery(id+"F8.wireOp",EDGE,"E25.0.7.0")])]}),"instanceName":"17"});
            var Q144;
            Q144=makeQuery(id+"F10.opPattern","COPY",BODY,{"derivedFrom":makeQuery(id+"F9.opExtrude","SWEPT_BODY",BODY,{"disambiguationData":[OSD([sQuery(id+"F8.wireOp",EDGE,"E24")])]}),"instanceName":"18"});
            var Q145;
            Q145=makeQuery(id+"F10.opPattern","COPY",BODY,{"derivedFrom":makeQuery(id+"F9.opExtrude","SWEPT_BODY",BODY,{"disambiguationData":[OSD([sQuery(id+"F8.wireOp",EDGE,"E25.0.1.0")])]}),"instanceName":"18"});
            var Q146;
            Q146=makeQuery(id+"F10.opPattern","COPY",BODY,{"derivedFrom":makeQuery(id+"F9.opExtrude","SWEPT_BODY",BODY,{"disambiguationData":[OSD([sQuery(id+"F8.wireOp",EDGE,"E25.0.2.0")])]}),"instanceName":"18"});
            var Q147;
            Q147=makeQuery(id+"F10.opPattern","COPY",BODY,{"derivedFrom":makeQuery(id+"F9.opExtrude","SWEPT_BODY",BODY,{"disambiguationData":[OSD([sQuery(id+"F8.wireOp",EDGE,"E25.0.3.0")])]}),"instanceName":"18"});
            var Q148;
            Q148=makeQuery(id+"F10.opPattern","COPY",BODY,{"derivedFrom":makeQuery(id+"F9.opExtrude","SWEPT_BODY",BODY,{"disambiguationData":[OSD([sQuery(id+"F8.wireOp",EDGE,"E25.0.4.0")])]}),"instanceName":"18"});
            var Q149;
            Q149=makeQuery(id+"F10.opPattern","COPY",BODY,{"derivedFrom":makeQuery(id+"F9.opExtrude","SWEPT_BODY",BODY,{"disambiguationData":[OSD([sQuery(id+"F8.wireOp",EDGE,"E25.0.5.0")])]}),"instanceName":"18"});
            var Q150;
            Q150=makeQuery(id+"F10.opPattern","COPY",BODY,{"derivedFrom":makeQuery(id+"F9.opExtrude","SWEPT_BODY",BODY,{"disambiguationData":[OSD([sQuery(id+"F8.wireOp",EDGE,"E25.0.6.0")])]}),"instanceName":"18"});
            var Q151;
            Q151=makeQuery(id+"F10.opPattern","COPY",BODY,{"derivedFrom":makeQuery(id+"F9.opExtrude","SWEPT_BODY",BODY,{"disambiguationData":[OSD([sQuery(id+"F8.wireOp",EDGE,"E25.0.7.0")])]}),"instanceName":"18"});
            var Q152;
            Q152=makeQuery(id+"F10.opPattern","COPY",BODY,{"derivedFrom":makeQuery(id+"F9.opExtrude","SWEPT_BODY",BODY,{"disambiguationData":[OSD([sQuery(id+"F8.wireOp",EDGE,"E24")])]}),"instanceName":"19"});
            var Q153;
            Q153=makeQuery(id+"F10.opPattern","COPY",BODY,{"derivedFrom":makeQuery(id+"F9.opExtrude","SWEPT_BODY",BODY,{"disambiguationData":[OSD([sQuery(id+"F8.wireOp",EDGE,"E25.0.1.0")])]}),"instanceName":"19"});
            var Q154;
            Q154=makeQuery(id+"F10.opPattern","COPY",BODY,{"derivedFrom":makeQuery(id+"F9.opExtrude","SWEPT_BODY",BODY,{"disambiguationData":[OSD([sQuery(id+"F8.wireOp",EDGE,"E25.0.2.0")])]}),"instanceName":"19"});
            var Q155;
            Q155=makeQuery(id+"F10.opPattern","COPY",BODY,{"derivedFrom":makeQuery(id+"F9.opExtrude","SWEPT_BODY",BODY,{"disambiguationData":[OSD([sQuery(id+"F8.wireOp",EDGE,"E25.0.3.0")])]}),"instanceName":"19"});
            var Q156;
            Q156=makeQuery(id+"F10.opPattern","COPY",BODY,{"derivedFrom":makeQuery(id+"F9.opExtrude","SWEPT_BODY",BODY,{"disambiguationData":[OSD([sQuery(id+"F8.wireOp",EDGE,"E25.0.4.0")])]}),"instanceName":"19"});
            var Q157;
            Q157=makeQuery(id+"F10.opPattern","COPY",BODY,{"derivedFrom":makeQuery(id+"F9.opExtrude","SWEPT_BODY",BODY,{"disambiguationData":[OSD([sQuery(id+"F8.wireOp",EDGE,"E25.0.5.0")])]}),"instanceName":"19"});
            var Q158;
            Q158=makeQuery(id+"F10.opPattern","COPY",BODY,{"derivedFrom":makeQuery(id+"F9.opExtrude","SWEPT_BODY",BODY,{"disambiguationData":[OSD([sQuery(id+"F8.wireOp",EDGE,"E25.0.6.0")])]}),"instanceName":"19"});
            var Q159;
            Q159=makeQuery(id+"F10.opPattern","COPY",BODY,{"derivedFrom":makeQuery(id+"F9.opExtrude","SWEPT_BODY",BODY,{"disambiguationData":[OSD([sQuery(id+"F8.wireOp",EDGE,"E25.0.7.0")])]}),"instanceName":"19"});
            var Q160;
            Q160=makeQuery(id+"F10.opPattern","COPY",BODY,{"derivedFrom":makeQuery(id+"F9.opExtrude","SWEPT_BODY",BODY,{"disambiguationData":[OSD([sQuery(id+"F8.wireOp",EDGE,"E24")])]}),"instanceName":"20"});
            var Q161;
            Q161=makeQuery(id+"F10.opPattern","COPY",BODY,{"derivedFrom":makeQuery(id+"F9.opExtrude","SWEPT_BODY",BODY,{"disambiguationData":[OSD([sQuery(id+"F8.wireOp",EDGE,"E25.0.1.0")])]}),"instanceName":"20"});
            var Q162;
            Q162=makeQuery(id+"F10.opPattern","COPY",BODY,{"derivedFrom":makeQuery(id+"F9.opExtrude","SWEPT_BODY",BODY,{"disambiguationData":[OSD([sQuery(id+"F8.wireOp",EDGE,"E25.0.2.0")])]}),"instanceName":"20"});
            var Q163;
            Q163=makeQuery(id+"F10.opPattern","COPY",BODY,{"derivedFrom":makeQuery(id+"F9.opExtrude","SWEPT_BODY",BODY,{"disambiguationData":[OSD([sQuery(id+"F8.wireOp",EDGE,"E25.0.3.0")])]}),"instanceName":"20"});
            var Q164;
            Q164=makeQuery(id+"F10.opPattern","COPY",BODY,{"derivedFrom":makeQuery(id+"F9.opExtrude","SWEPT_BODY",BODY,{"disambiguationData":[OSD([sQuery(id+"F8.wireOp",EDGE,"E25.0.4.0")])]}),"instanceName":"20"});
            var Q165;
            Q165=makeQuery(id+"F10.opPattern","COPY",BODY,{"derivedFrom":makeQuery(id+"F9.opExtrude","SWEPT_BODY",BODY,{"disambiguationData":[OSD([sQuery(id+"F8.wireOp",EDGE,"E25.0.5.0")])]}),"instanceName":"20"});
            var Q166;
            Q166=makeQuery(id+"F10.opPattern","COPY",BODY,{"derivedFrom":makeQuery(id+"F9.opExtrude","SWEPT_BODY",BODY,{"disambiguationData":[OSD([sQuery(id+"F8.wireOp",EDGE,"E25.0.6.0")])]}),"instanceName":"20"});
            var Q167;
            Q167=makeQuery(id+"F10.opPattern","COPY",BODY,{"derivedFrom":makeQuery(id+"F9.opExtrude","SWEPT_BODY",BODY,{"disambiguationData":[OSD([sQuery(id+"F8.wireOp",EDGE,"E25.0.7.0")])]}),"instanceName":"20"});
            var Q168;
            Q168=makeQuery(id+"F10.opPattern","COPY",BODY,{"derivedFrom":makeQuery(id+"F9.opExtrude","SWEPT_BODY",BODY,{"disambiguationData":[OSD([sQuery(id+"F8.wireOp",EDGE,"E24")])]}),"instanceName":"21"});
            var Q169;
            Q169=makeQuery(id+"F10.opPattern","COPY",BODY,{"derivedFrom":makeQuery(id+"F9.opExtrude","SWEPT_BODY",BODY,{"disambiguationData":[OSD([sQuery(id+"F8.wireOp",EDGE,"E25.0.1.0")])]}),"instanceName":"21"});
            var Q170;
            Q170=makeQuery(id+"F10.opPattern","COPY",BODY,{"derivedFrom":makeQuery(id+"F9.opExtrude","SWEPT_BODY",BODY,{"disambiguationData":[OSD([sQuery(id+"F8.wireOp",EDGE,"E25.0.2.0")])]}),"instanceName":"21"});
            var Q171;
            Q171=makeQuery(id+"F10.opPattern","COPY",BODY,{"derivedFrom":makeQuery(id+"F9.opExtrude","SWEPT_BODY",BODY,{"disambiguationData":[OSD([sQuery(id+"F8.wireOp",EDGE,"E25.0.3.0")])]}),"instanceName":"21"});
            var Q172;
            Q172=makeQuery(id+"F10.opPattern","COPY",BODY,{"derivedFrom":makeQuery(id+"F9.opExtrude","SWEPT_BODY",BODY,{"disambiguationData":[OSD([sQuery(id+"F8.wireOp",EDGE,"E25.0.4.0")])]}),"instanceName":"21"});
            var Q173;
            Q173=makeQuery(id+"F10.opPattern","COPY",BODY,{"derivedFrom":makeQuery(id+"F9.opExtrude","SWEPT_BODY",BODY,{"disambiguationData":[OSD([sQuery(id+"F8.wireOp",EDGE,"E25.0.5.0")])]}),"instanceName":"21"});
            var Q174;
            Q174=makeQuery(id+"F10.opPattern","COPY",BODY,{"derivedFrom":makeQuery(id+"F9.opExtrude","SWEPT_BODY",BODY,{"disambiguationData":[OSD([sQuery(id+"F8.wireOp",EDGE,"E25.0.6.0")])]}),"instanceName":"21"});
            var Q175;
            Q175=makeQuery(id+"F10.opPattern","COPY",BODY,{"derivedFrom":makeQuery(id+"F9.opExtrude","SWEPT_BODY",BODY,{"disambiguationData":[OSD([sQuery(id+"F8.wireOp",EDGE,"E25.0.7.0")])]}),"instanceName":"21"});
            var Q176;
            Q176=makeQuery(id+"F10.opPattern","COPY",BODY,{"derivedFrom":makeQuery(id+"F9.opExtrude","SWEPT_BODY",BODY,{"disambiguationData":[OSD([sQuery(id+"F8.wireOp",EDGE,"E24")])]}),"instanceName":"22"});
            var Q177;
            Q177=makeQuery(id+"F10.opPattern","COPY",BODY,{"derivedFrom":makeQuery(id+"F9.opExtrude","SWEPT_BODY",BODY,{"disambiguationData":[OSD([sQuery(id+"F8.wireOp",EDGE,"E25.0.1.0")])]}),"instanceName":"22"});
            var Q178;
            Q178=makeQuery(id+"F10.opPattern","COPY",BODY,{"derivedFrom":makeQuery(id+"F9.opExtrude","SWEPT_BODY",BODY,{"disambiguationData":[OSD([sQuery(id+"F8.wireOp",EDGE,"E25.0.2.0")])]}),"instanceName":"22"});
            var Q179;
            Q179=makeQuery(id+"F10.opPattern","COPY",BODY,{"derivedFrom":makeQuery(id+"F9.opExtrude","SWEPT_BODY",BODY,{"disambiguationData":[OSD([sQuery(id+"F8.wireOp",EDGE,"E25.0.3.0")])]}),"instanceName":"22"});
            var Q180;
            Q180=makeQuery(id+"F10.opPattern","COPY",BODY,{"derivedFrom":makeQuery(id+"F9.opExtrude","SWEPT_BODY",BODY,{"disambiguationData":[OSD([sQuery(id+"F8.wireOp",EDGE,"E25.0.4.0")])]}),"instanceName":"22"});
            var Q181;
            Q181=makeQuery(id+"F10.opPattern","COPY",BODY,{"derivedFrom":makeQuery(id+"F9.opExtrude","SWEPT_BODY",BODY,{"disambiguationData":[OSD([sQuery(id+"F8.wireOp",EDGE,"E25.0.5.0")])]}),"instanceName":"22"});
            var Q182;
            Q182=makeQuery(id+"F10.opPattern","COPY",BODY,{"derivedFrom":makeQuery(id+"F9.opExtrude","SWEPT_BODY",BODY,{"disambiguationData":[OSD([sQuery(id+"F8.wireOp",EDGE,"E25.0.6.0")])]}),"instanceName":"22"});
            var Q183;
            Q183=makeQuery(id+"F10.opPattern","COPY",BODY,{"derivedFrom":makeQuery(id+"F9.opExtrude","SWEPT_BODY",BODY,{"disambiguationData":[OSD([sQuery(id+"F8.wireOp",EDGE,"E25.0.7.0")])]}),"instanceName":"22"});
            var Q184;
            Q184=makeQuery(id+"F10.opPattern","COPY",BODY,{"derivedFrom":makeQuery(id+"F9.opExtrude","SWEPT_BODY",BODY,{"disambiguationData":[OSD([sQuery(id+"F8.wireOp",EDGE,"E24")])]}),"instanceName":"23"});
            var Q185;
            Q185=makeQuery(id+"F10.opPattern","COPY",BODY,{"derivedFrom":makeQuery(id+"F9.opExtrude","SWEPT_BODY",BODY,{"disambiguationData":[OSD([sQuery(id+"F8.wireOp",EDGE,"E25.0.1.0")])]}),"instanceName":"23"});
            var Q186;
            Q186=makeQuery(id+"F10.opPattern","COPY",BODY,{"derivedFrom":makeQuery(id+"F9.opExtrude","SWEPT_BODY",BODY,{"disambiguationData":[OSD([sQuery(id+"F8.wireOp",EDGE,"E25.0.2.0")])]}),"instanceName":"23"});
            var Q187;
            Q187=makeQuery(id+"F10.opPattern","COPY",BODY,{"derivedFrom":makeQuery(id+"F9.opExtrude","SWEPT_BODY",BODY,{"disambiguationData":[OSD([sQuery(id+"F8.wireOp",EDGE,"E25.0.3.0")])]}),"instanceName":"23"});
            var Q188;
            Q188=makeQuery(id+"F10.opPattern","COPY",BODY,{"derivedFrom":makeQuery(id+"F9.opExtrude","SWEPT_BODY",BODY,{"disambiguationData":[OSD([sQuery(id+"F8.wireOp",EDGE,"E25.0.4.0")])]}),"instanceName":"23"});
            var Q189;
            Q189=makeQuery(id+"F10.opPattern","COPY",BODY,{"derivedFrom":makeQuery(id+"F9.opExtrude","SWEPT_BODY",BODY,{"disambiguationData":[OSD([sQuery(id+"F8.wireOp",EDGE,"E25.0.5.0")])]}),"instanceName":"23"});
            var Q190;
            Q190=makeQuery(id+"F10.opPattern","COPY",BODY,{"derivedFrom":makeQuery(id+"F9.opExtrude","SWEPT_BODY",BODY,{"disambiguationData":[OSD([sQuery(id+"F8.wireOp",EDGE,"E25.0.6.0")])]}),"instanceName":"23"});
            var Q191;
            Q191=makeQuery(id+"F10.opPattern","COPY",BODY,{"derivedFrom":makeQuery(id+"F9.opExtrude","SWEPT_BODY",BODY,{"disambiguationData":[OSD([sQuery(id+"F8.wireOp",EDGE,"E25.0.7.0")])]}),"instanceName":"23"});
            var Q192;
            Q192=makeQuery(id+"F10.opPattern","COPY",BODY,{"derivedFrom":makeQuery(id+"F9.opExtrude","SWEPT_BODY",BODY,{"disambiguationData":[OSD([sQuery(id+"F8.wireOp",EDGE,"E24")])]}),"instanceName":"24"});
            var Q193;
            Q193=makeQuery(id+"F10.opPattern","COPY",BODY,{"derivedFrom":makeQuery(id+"F9.opExtrude","SWEPT_BODY",BODY,{"disambiguationData":[OSD([sQuery(id+"F8.wireOp",EDGE,"E25.0.1.0")])]}),"instanceName":"24"});
            var Q194;
            Q194=makeQuery(id+"F10.opPattern","COPY",BODY,{"derivedFrom":makeQuery(id+"F9.opExtrude","SWEPT_BODY",BODY,{"disambiguationData":[OSD([sQuery(id+"F8.wireOp",EDGE,"E25.0.2.0")])]}),"instanceName":"24"});
            var Q195;
            Q195=makeQuery(id+"F10.opPattern","COPY",BODY,{"derivedFrom":makeQuery(id+"F9.opExtrude","SWEPT_BODY",BODY,{"disambiguationData":[OSD([sQuery(id+"F8.wireOp",EDGE,"E25.0.3.0")])]}),"instanceName":"24"});
            var Q196;
            Q196=makeQuery(id+"F10.opPattern","COPY",BODY,{"derivedFrom":makeQuery(id+"F9.opExtrude","SWEPT_BODY",BODY,{"disambiguationData":[OSD([sQuery(id+"F8.wireOp",EDGE,"E25.0.4.0")])]}),"instanceName":"24"});
            var Q197;
            Q197=makeQuery(id+"F10.opPattern","COPY",BODY,{"derivedFrom":makeQuery(id+"F9.opExtrude","SWEPT_BODY",BODY,{"disambiguationData":[OSD([sQuery(id+"F8.wireOp",EDGE,"E25.0.5.0")])]}),"instanceName":"24"});
            var Q198;
            Q198=makeQuery(id+"F10.opPattern","COPY",BODY,{"derivedFrom":makeQuery(id+"F9.opExtrude","SWEPT_BODY",BODY,{"disambiguationData":[OSD([sQuery(id+"F8.wireOp",EDGE,"E25.0.6.0")])]}),"instanceName":"24"});
            var Q199;
            Q199=makeQuery(id+"F10.opPattern","COPY",BODY,{"derivedFrom":makeQuery(id+"F9.opExtrude","SWEPT_BODY",BODY,{"disambiguationData":[OSD([sQuery(id+"F8.wireOp",EDGE,"E25.0.7.0")])]}),"instanceName":"24"});
            var Q200;
            Q200=makeQuery(id+"F10.opPattern","COPY",BODY,{"derivedFrom":makeQuery(id+"F9.opExtrude","SWEPT_BODY",BODY,{"disambiguationData":[OSD([sQuery(id+"F8.wireOp",EDGE,"E24")])]}),"instanceName":"25"});
            var Q201;
            Q201=makeQuery(id+"F10.opPattern","COPY",BODY,{"derivedFrom":makeQuery(id+"F9.opExtrude","SWEPT_BODY",BODY,{"disambiguationData":[OSD([sQuery(id+"F8.wireOp",EDGE,"E25.0.1.0")])]}),"instanceName":"25"});
            var Q202;
            Q202=makeQuery(id+"F10.opPattern","COPY",BODY,{"derivedFrom":makeQuery(id+"F9.opExtrude","SWEPT_BODY",BODY,{"disambiguationData":[OSD([sQuery(id+"F8.wireOp",EDGE,"E25.0.2.0")])]}),"instanceName":"25"});
            var Q203;
            Q203=makeQuery(id+"F10.opPattern","COPY",BODY,{"derivedFrom":makeQuery(id+"F9.opExtrude","SWEPT_BODY",BODY,{"disambiguationData":[OSD([sQuery(id+"F8.wireOp",EDGE,"E25.0.3.0")])]}),"instanceName":"25"});
            var Q204;
            Q204=makeQuery(id+"F10.opPattern","COPY",BODY,{"derivedFrom":makeQuery(id+"F9.opExtrude","SWEPT_BODY",BODY,{"disambiguationData":[OSD([sQuery(id+"F8.wireOp",EDGE,"E25.0.4.0")])]}),"instanceName":"25"});
            var Q205;
            Q205=makeQuery(id+"F10.opPattern","COPY",BODY,{"derivedFrom":makeQuery(id+"F9.opExtrude","SWEPT_BODY",BODY,{"disambiguationData":[OSD([sQuery(id+"F8.wireOp",EDGE,"E25.0.5.0")])]}),"instanceName":"25"});
            var Q206;
            Q206=makeQuery(id+"F10.opPattern","COPY",BODY,{"derivedFrom":makeQuery(id+"F9.opExtrude","SWEPT_BODY",BODY,{"disambiguationData":[OSD([sQuery(id+"F8.wireOp",EDGE,"E25.0.6.0")])]}),"instanceName":"25"});
            var Q207;
            Q207=makeQuery(id+"F10.opPattern","COPY",BODY,{"derivedFrom":makeQuery(id+"F9.opExtrude","SWEPT_BODY",BODY,{"disambiguationData":[OSD([sQuery(id+"F8.wireOp",EDGE,"E25.0.7.0")])]}),"instanceName":"25"});
            var Q208;
            Q208=makeQuery(id+"F10.opPattern","COPY",BODY,{"derivedFrom":makeQuery(id+"F9.opExtrude","SWEPT_BODY",BODY,{"disambiguationData":[OSD([sQuery(id+"F8.wireOp",EDGE,"E24")])]}),"instanceName":"26"});
            var Q209;
            Q209=makeQuery(id+"F10.opPattern","COPY",BODY,{"derivedFrom":makeQuery(id+"F9.opExtrude","SWEPT_BODY",BODY,{"disambiguationData":[OSD([sQuery(id+"F8.wireOp",EDGE,"E25.0.1.0")])]}),"instanceName":"26"});
            var Q210;
            Q210=makeQuery(id+"F10.opPattern","COPY",BODY,{"derivedFrom":makeQuery(id+"F9.opExtrude","SWEPT_BODY",BODY,{"disambiguationData":[OSD([sQuery(id+"F8.wireOp",EDGE,"E25.0.2.0")])]}),"instanceName":"26"});
            var Q211;
            Q211=makeQuery(id+"F10.opPattern","COPY",BODY,{"derivedFrom":makeQuery(id+"F9.opExtrude","SWEPT_BODY",BODY,{"disambiguationData":[OSD([sQuery(id+"F8.wireOp",EDGE,"E25.0.3.0")])]}),"instanceName":"26"});
            var Q212;
            Q212=makeQuery(id+"F10.opPattern","COPY",BODY,{"derivedFrom":makeQuery(id+"F9.opExtrude","SWEPT_BODY",BODY,{"disambiguationData":[OSD([sQuery(id+"F8.wireOp",EDGE,"E25.0.4.0")])]}),"instanceName":"26"});
            var Q213;
            Q213=makeQuery(id+"F10.opPattern","COPY",BODY,{"derivedFrom":makeQuery(id+"F9.opExtrude","SWEPT_BODY",BODY,{"disambiguationData":[OSD([sQuery(id+"F8.wireOp",EDGE,"E25.0.5.0")])]}),"instanceName":"26"});
            var Q214;
            Q214=makeQuery(id+"F10.opPattern","COPY",BODY,{"derivedFrom":makeQuery(id+"F9.opExtrude","SWEPT_BODY",BODY,{"disambiguationData":[OSD([sQuery(id+"F8.wireOp",EDGE,"E25.0.6.0")])]}),"instanceName":"26"});
            var Q215;
            Q215=makeQuery(id+"F10.opPattern","COPY",BODY,{"derivedFrom":makeQuery(id+"F9.opExtrude","SWEPT_BODY",BODY,{"disambiguationData":[OSD([sQuery(id+"F8.wireOp",EDGE,"E25.0.7.0")])]}),"instanceName":"26"});
            var Q216;
            Q216=makeQuery(id+"F10.opPattern","COPY",BODY,{"derivedFrom":makeQuery(id+"F9.opExtrude","SWEPT_BODY",BODY,{"disambiguationData":[OSD([sQuery(id+"F8.wireOp",EDGE,"E24")])]}),"instanceName":"27"});
            var Q217;
            Q217=makeQuery(id+"F10.opPattern","COPY",BODY,{"derivedFrom":makeQuery(id+"F9.opExtrude","SWEPT_BODY",BODY,{"disambiguationData":[OSD([sQuery(id+"F8.wireOp",EDGE,"E25.0.1.0")])]}),"instanceName":"27"});
            var Q218;
            Q218=makeQuery(id+"F10.opPattern","COPY",BODY,{"derivedFrom":makeQuery(id+"F9.opExtrude","SWEPT_BODY",BODY,{"disambiguationData":[OSD([sQuery(id+"F8.wireOp",EDGE,"E25.0.2.0")])]}),"instanceName":"27"});
            var Q219;
            Q219=makeQuery(id+"F10.opPattern","COPY",BODY,{"derivedFrom":makeQuery(id+"F9.opExtrude","SWEPT_BODY",BODY,{"disambiguationData":[OSD([sQuery(id+"F8.wireOp",EDGE,"E25.0.3.0")])]}),"instanceName":"27"});
            var Q220;
            Q220=makeQuery(id+"F10.opPattern","COPY",BODY,{"derivedFrom":makeQuery(id+"F9.opExtrude","SWEPT_BODY",BODY,{"disambiguationData":[OSD([sQuery(id+"F8.wireOp",EDGE,"E25.0.4.0")])]}),"instanceName":"27"});
            var Q221;
            Q221=makeQuery(id+"F10.opPattern","COPY",BODY,{"derivedFrom":makeQuery(id+"F9.opExtrude","SWEPT_BODY",BODY,{"disambiguationData":[OSD([sQuery(id+"F8.wireOp",EDGE,"E25.0.5.0")])]}),"instanceName":"27"});
            var Q222;
            Q222=makeQuery(id+"F10.opPattern","COPY",BODY,{"derivedFrom":makeQuery(id+"F9.opExtrude","SWEPT_BODY",BODY,{"disambiguationData":[OSD([sQuery(id+"F8.wireOp",EDGE,"E25.0.6.0")])]}),"instanceName":"27"});
            var Q223;
            Q223=makeQuery(id+"F10.opPattern","COPY",BODY,{"derivedFrom":makeQuery(id+"F9.opExtrude","SWEPT_BODY",BODY,{"disambiguationData":[OSD([sQuery(id+"F8.wireOp",EDGE,"E25.0.7.0")])]}),"instanceName":"27"});
            var Q224;
            Q224=makeQuery(id+"F10.opPattern","COPY",BODY,{"derivedFrom":makeQuery(id+"F9.opExtrude","SWEPT_BODY",BODY,{"disambiguationData":[OSD([sQuery(id+"F8.wireOp",EDGE,"E24")])]}),"instanceName":"28"});
            var Q225;
            Q225=makeQuery(id+"F10.opPattern","COPY",BODY,{"derivedFrom":makeQuery(id+"F9.opExtrude","SWEPT_BODY",BODY,{"disambiguationData":[OSD([sQuery(id+"F8.wireOp",EDGE,"E25.0.1.0")])]}),"instanceName":"28"});
            var Q226;
            Q226=makeQuery(id+"F10.opPattern","COPY",BODY,{"derivedFrom":makeQuery(id+"F9.opExtrude","SWEPT_BODY",BODY,{"disambiguationData":[OSD([sQuery(id+"F8.wireOp",EDGE,"E25.0.2.0")])]}),"instanceName":"28"});
            var Q227;
            Q227=makeQuery(id+"F10.opPattern","COPY",BODY,{"derivedFrom":makeQuery(id+"F9.opExtrude","SWEPT_BODY",BODY,{"disambiguationData":[OSD([sQuery(id+"F8.wireOp",EDGE,"E25.0.3.0")])]}),"instanceName":"28"});
            var Q228;
            Q228=makeQuery(id+"F10.opPattern","COPY",BODY,{"derivedFrom":makeQuery(id+"F9.opExtrude","SWEPT_BODY",BODY,{"disambiguationData":[OSD([sQuery(id+"F8.wireOp",EDGE,"E25.0.4.0")])]}),"instanceName":"28"});
            var Q229;
            Q229=makeQuery(id+"F10.opPattern","COPY",BODY,{"derivedFrom":makeQuery(id+"F9.opExtrude","SWEPT_BODY",BODY,{"disambiguationData":[OSD([sQuery(id+"F8.wireOp",EDGE,"E25.0.5.0")])]}),"instanceName":"28"});
            var Q230;
            Q230=makeQuery(id+"F10.opPattern","COPY",BODY,{"derivedFrom":makeQuery(id+"F9.opExtrude","SWEPT_BODY",BODY,{"disambiguationData":[OSD([sQuery(id+"F8.wireOp",EDGE,"E25.0.6.0")])]}),"instanceName":"28"});
            var Q231;
            Q231=makeQuery(id+"F10.opPattern","COPY",BODY,{"derivedFrom":makeQuery(id+"F9.opExtrude","SWEPT_BODY",BODY,{"disambiguationData":[OSD([sQuery(id+"F8.wireOp",EDGE,"E25.0.7.0")])]}),"instanceName":"28"});
            var Q232;
            Q232=makeQuery(id+"F10.opPattern","COPY",BODY,{"derivedFrom":makeQuery(id+"F9.opExtrude","SWEPT_BODY",BODY,{"disambiguationData":[OSD([sQuery(id+"F8.wireOp",EDGE,"E24")])]}),"instanceName":"29"});
            var Q233;
            Q233=makeQuery(id+"F10.opPattern","COPY",BODY,{"derivedFrom":makeQuery(id+"F9.opExtrude","SWEPT_BODY",BODY,{"disambiguationData":[OSD([sQuery(id+"F8.wireOp",EDGE,"E25.0.1.0")])]}),"instanceName":"29"});
            var Q234;
            Q234=makeQuery(id+"F10.opPattern","COPY",BODY,{"derivedFrom":makeQuery(id+"F9.opExtrude","SWEPT_BODY",BODY,{"disambiguationData":[OSD([sQuery(id+"F8.wireOp",EDGE,"E25.0.2.0")])]}),"instanceName":"29"});
            var Q235;
            Q235=makeQuery(id+"F10.opPattern","COPY",BODY,{"derivedFrom":makeQuery(id+"F9.opExtrude","SWEPT_BODY",BODY,{"disambiguationData":[OSD([sQuery(id+"F8.wireOp",EDGE,"E25.0.3.0")])]}),"instanceName":"29"});
            var Q236;
            Q236=makeQuery(id+"F10.opPattern","COPY",BODY,{"derivedFrom":makeQuery(id+"F9.opExtrude","SWEPT_BODY",BODY,{"disambiguationData":[OSD([sQuery(id+"F8.wireOp",EDGE,"E25.0.4.0")])]}),"instanceName":"29"});
            var Q237;
            Q237=makeQuery(id+"F10.opPattern","COPY",BODY,{"derivedFrom":makeQuery(id+"F9.opExtrude","SWEPT_BODY",BODY,{"disambiguationData":[OSD([sQuery(id+"F8.wireOp",EDGE,"E25.0.5.0")])]}),"instanceName":"29"});
            var Q238;
            Q238=makeQuery(id+"F10.opPattern","COPY",BODY,{"derivedFrom":makeQuery(id+"F9.opExtrude","SWEPT_BODY",BODY,{"disambiguationData":[OSD([sQuery(id+"F8.wireOp",EDGE,"E25.0.6.0")])]}),"instanceName":"29"});
            var Q239;
            Q239=makeQuery(id+"F10.opPattern","COPY",BODY,{"derivedFrom":makeQuery(id+"F9.opExtrude","SWEPT_BODY",BODY,{"disambiguationData":[OSD([sQuery(id+"F8.wireOp",EDGE,"E25.0.7.0")])]}),"instanceName":"29"});
            var Q240;
            Q240=makeQuery(id+"F10.opPattern","COPY",BODY,{"derivedFrom":makeQuery(id+"F9.opExtrude","SWEPT_BODY",BODY,{"disambiguationData":[OSD([sQuery(id+"F8.wireOp",EDGE,"E24")])]}),"instanceName":"30"});
            var Q241;
            Q241=makeQuery(id+"F10.opPattern","COPY",BODY,{"derivedFrom":makeQuery(id+"F9.opExtrude","SWEPT_BODY",BODY,{"disambiguationData":[OSD([sQuery(id+"F8.wireOp",EDGE,"E25.0.1.0")])]}),"instanceName":"30"});
            var Q242;
            Q242=makeQuery(id+"F10.opPattern","COPY",BODY,{"derivedFrom":makeQuery(id+"F9.opExtrude","SWEPT_BODY",BODY,{"disambiguationData":[OSD([sQuery(id+"F8.wireOp",EDGE,"E25.0.2.0")])]}),"instanceName":"30"});
            var Q243;
            Q243=makeQuery(id+"F10.opPattern","COPY",BODY,{"derivedFrom":makeQuery(id+"F9.opExtrude","SWEPT_BODY",BODY,{"disambiguationData":[OSD([sQuery(id+"F8.wireOp",EDGE,"E25.0.3.0")])]}),"instanceName":"30"});
            var Q244;
            Q244=makeQuery(id+"F10.opPattern","COPY",BODY,{"derivedFrom":makeQuery(id+"F9.opExtrude","SWEPT_BODY",BODY,{"disambiguationData":[OSD([sQuery(id+"F8.wireOp",EDGE,"E25.0.4.0")])]}),"instanceName":"30"});
            var Q245;
            Q245=makeQuery(id+"F10.opPattern","COPY",BODY,{"derivedFrom":makeQuery(id+"F9.opExtrude","SWEPT_BODY",BODY,{"disambiguationData":[OSD([sQuery(id+"F8.wireOp",EDGE,"E25.0.5.0")])]}),"instanceName":"30"});
            var Q246;
            Q246=makeQuery(id+"F10.opPattern","COPY",BODY,{"derivedFrom":makeQuery(id+"F9.opExtrude","SWEPT_BODY",BODY,{"disambiguationData":[OSD([sQuery(id+"F8.wireOp",EDGE,"E25.0.6.0")])]}),"instanceName":"30"});
            var Q247;
            Q247=makeQuery(id+"F10.opPattern","COPY",BODY,{"derivedFrom":makeQuery(id+"F9.opExtrude","SWEPT_BODY",BODY,{"disambiguationData":[OSD([sQuery(id+"F8.wireOp",EDGE,"E25.0.7.0")])]}),"instanceName":"30"});
            var Q248;
            Q248=makeQuery(id+"F10.opPattern","COPY",BODY,{"derivedFrom":makeQuery(id+"F9.opExtrude","SWEPT_BODY",BODY,{"disambiguationData":[OSD([sQuery(id+"F8.wireOp",EDGE,"E24")])]}),"instanceName":"31"});
            var Q249;
            Q249=makeQuery(id+"F10.opPattern","COPY",BODY,{"derivedFrom":makeQuery(id+"F9.opExtrude","SWEPT_BODY",BODY,{"disambiguationData":[OSD([sQuery(id+"F8.wireOp",EDGE,"E25.0.1.0")])]}),"instanceName":"31"});
            var Q250;
            Q250=makeQuery(id+"F10.opPattern","COPY",BODY,{"derivedFrom":makeQuery(id+"F9.opExtrude","SWEPT_BODY",BODY,{"disambiguationData":[OSD([sQuery(id+"F8.wireOp",EDGE,"E25.0.2.0")])]}),"instanceName":"31"});
            var Q251;
            Q251=makeQuery(id+"F10.opPattern","COPY",BODY,{"derivedFrom":makeQuery(id+"F9.opExtrude","SWEPT_BODY",BODY,{"disambiguationData":[OSD([sQuery(id+"F8.wireOp",EDGE,"E25.0.3.0")])]}),"instanceName":"31"});
            var Q252;
            Q252=makeQuery(id+"F10.opPattern","COPY",BODY,{"derivedFrom":makeQuery(id+"F9.opExtrude","SWEPT_BODY",BODY,{"disambiguationData":[OSD([sQuery(id+"F8.wireOp",EDGE,"E25.0.4.0")])]}),"instanceName":"31"});
            var Q253;
            Q253=makeQuery(id+"F10.opPattern","COPY",BODY,{"derivedFrom":makeQuery(id+"F9.opExtrude","SWEPT_BODY",BODY,{"disambiguationData":[OSD([sQuery(id+"F8.wireOp",EDGE,"E25.0.5.0")])]}),"instanceName":"31"});
            var Q254;
            Q254=makeQuery(id+"F10.opPattern","COPY",BODY,{"derivedFrom":makeQuery(id+"F9.opExtrude","SWEPT_BODY",BODY,{"disambiguationData":[OSD([sQuery(id+"F8.wireOp",EDGE,"E25.0.6.0")])]}),"instanceName":"31"});
            var Q255;
            Q255=makeQuery(id+"F10.opPattern","COPY",BODY,{"derivedFrom":makeQuery(id+"F9.opExtrude","SWEPT_BODY",BODY,{"disambiguationData":[OSD([sQuery(id+"F8.wireOp",EDGE,"E25.0.7.0")])]}),"instanceName":"31"});
            var Q256;
            Q256=makeQuery(id+"F10.opPattern","COPY",BODY,{"derivedFrom":makeQuery(id+"F9.opExtrude","SWEPT_BODY",BODY,{"disambiguationData":[OSD([sQuery(id+"F8.wireOp",EDGE,"E24")])]}),"instanceName":"32"});
            var Q257;
            Q257=makeQuery(id+"F10.opPattern","COPY",BODY,{"derivedFrom":makeQuery(id+"F9.opExtrude","SWEPT_BODY",BODY,{"disambiguationData":[OSD([sQuery(id+"F8.wireOp",EDGE,"E25.0.1.0")])]}),"instanceName":"32"});
            var Q258;
            Q258=makeQuery(id+"F10.opPattern","COPY",BODY,{"derivedFrom":makeQuery(id+"F9.opExtrude","SWEPT_BODY",BODY,{"disambiguationData":[OSD([sQuery(id+"F8.wireOp",EDGE,"E25.0.2.0")])]}),"instanceName":"32"});
            var Q259;
            Q259=makeQuery(id+"F10.opPattern","COPY",BODY,{"derivedFrom":makeQuery(id+"F9.opExtrude","SWEPT_BODY",BODY,{"disambiguationData":[OSD([sQuery(id+"F8.wireOp",EDGE,"E25.0.3.0")])]}),"instanceName":"32"});
            var Q260;
            Q260=makeQuery(id+"F10.opPattern","COPY",BODY,{"derivedFrom":makeQuery(id+"F9.opExtrude","SWEPT_BODY",BODY,{"disambiguationData":[OSD([sQuery(id+"F8.wireOp",EDGE,"E25.0.4.0")])]}),"instanceName":"32"});
            var Q261;
            Q261=makeQuery(id+"F10.opPattern","COPY",BODY,{"derivedFrom":makeQuery(id+"F9.opExtrude","SWEPT_BODY",BODY,{"disambiguationData":[OSD([sQuery(id+"F8.wireOp",EDGE,"E25.0.5.0")])]}),"instanceName":"32"});
            var Q262;
            Q262=makeQuery(id+"F10.opPattern","COPY",BODY,{"derivedFrom":makeQuery(id+"F9.opExtrude","SWEPT_BODY",BODY,{"disambiguationData":[OSD([sQuery(id+"F8.wireOp",EDGE,"E25.0.6.0")])]}),"instanceName":"32"});
            var Q263;
            Q263=makeQuery(id+"F10.opPattern","COPY",BODY,{"derivedFrom":makeQuery(id+"F9.opExtrude","SWEPT_BODY",BODY,{"disambiguationData":[OSD([sQuery(id+"F8.wireOp",EDGE,"E25.0.7.0")])]}),"instanceName":"32"});
            var Q264;
            Q264=makeQuery(id+"F10.opPattern","COPY",BODY,{"derivedFrom":makeQuery(id+"F9.opExtrude","SWEPT_BODY",BODY,{"disambiguationData":[OSD([sQuery(id+"F8.wireOp",EDGE,"E24")])]}),"instanceName":"33"});
            var Q265;
            Q265=makeQuery(id+"F10.opPattern","COPY",BODY,{"derivedFrom":makeQuery(id+"F9.opExtrude","SWEPT_BODY",BODY,{"disambiguationData":[OSD([sQuery(id+"F8.wireOp",EDGE,"E25.0.1.0")])]}),"instanceName":"33"});
            var Q266;
            Q266=makeQuery(id+"F10.opPattern","COPY",BODY,{"derivedFrom":makeQuery(id+"F9.opExtrude","SWEPT_BODY",BODY,{"disambiguationData":[OSD([sQuery(id+"F8.wireOp",EDGE,"E25.0.2.0")])]}),"instanceName":"33"});
            var Q267;
            Q267=makeQuery(id+"F10.opPattern","COPY",BODY,{"derivedFrom":makeQuery(id+"F9.opExtrude","SWEPT_BODY",BODY,{"disambiguationData":[OSD([sQuery(id+"F8.wireOp",EDGE,"E25.0.3.0")])]}),"instanceName":"33"});
            var Q268;
            Q268=makeQuery(id+"F10.opPattern","COPY",BODY,{"derivedFrom":makeQuery(id+"F9.opExtrude","SWEPT_BODY",BODY,{"disambiguationData":[OSD([sQuery(id+"F8.wireOp",EDGE,"E25.0.4.0")])]}),"instanceName":"33"});
            var Q269;
            Q269=makeQuery(id+"F10.opPattern","COPY",BODY,{"derivedFrom":makeQuery(id+"F9.opExtrude","SWEPT_BODY",BODY,{"disambiguationData":[OSD([sQuery(id+"F8.wireOp",EDGE,"E25.0.5.0")])]}),"instanceName":"33"});
            var Q270;
            Q270=makeQuery(id+"F10.opPattern","COPY",BODY,{"derivedFrom":makeQuery(id+"F9.opExtrude","SWEPT_BODY",BODY,{"disambiguationData":[OSD([sQuery(id+"F8.wireOp",EDGE,"E25.0.6.0")])]}),"instanceName":"33"});
            var Q271;
            Q271=makeQuery(id+"F10.opPattern","COPY",BODY,{"derivedFrom":makeQuery(id+"F9.opExtrude","SWEPT_BODY",BODY,{"disambiguationData":[OSD([sQuery(id+"F8.wireOp",EDGE,"E25.0.7.0")])]}),"instanceName":"33"});
            var Q272;
            Q272=makeQuery(id+"F10.opPattern","COPY",BODY,{"derivedFrom":makeQuery(id+"F9.opExtrude","SWEPT_BODY",BODY,{"disambiguationData":[OSD([sQuery(id+"F8.wireOp",EDGE,"E24")])]}),"instanceName":"34"});
            var Q273;
            Q273=makeQuery(id+"F10.opPattern","COPY",BODY,{"derivedFrom":makeQuery(id+"F9.opExtrude","SWEPT_BODY",BODY,{"disambiguationData":[OSD([sQuery(id+"F8.wireOp",EDGE,"E25.0.1.0")])]}),"instanceName":"34"});
            var Q274;
            Q274=makeQuery(id+"F10.opPattern","COPY",BODY,{"derivedFrom":makeQuery(id+"F9.opExtrude","SWEPT_BODY",BODY,{"disambiguationData":[OSD([sQuery(id+"F8.wireOp",EDGE,"E25.0.2.0")])]}),"instanceName":"34"});
            var Q275;
            Q275=makeQuery(id+"F10.opPattern","COPY",BODY,{"derivedFrom":makeQuery(id+"F9.opExtrude","SWEPT_BODY",BODY,{"disambiguationData":[OSD([sQuery(id+"F8.wireOp",EDGE,"E25.0.3.0")])]}),"instanceName":"34"});
            var Q276;
            Q276=makeQuery(id+"F10.opPattern","COPY",BODY,{"derivedFrom":makeQuery(id+"F9.opExtrude","SWEPT_BODY",BODY,{"disambiguationData":[OSD([sQuery(id+"F8.wireOp",EDGE,"E25.0.4.0")])]}),"instanceName":"34"});
            var Q277;
            Q277=makeQuery(id+"F10.opPattern","COPY",BODY,{"derivedFrom":makeQuery(id+"F9.opExtrude","SWEPT_BODY",BODY,{"disambiguationData":[OSD([sQuery(id+"F8.wireOp",EDGE,"E25.0.5.0")])]}),"instanceName":"34"});
            var Q278;
            Q278=makeQuery(id+"F10.opPattern","COPY",BODY,{"derivedFrom":makeQuery(id+"F9.opExtrude","SWEPT_BODY",BODY,{"disambiguationData":[OSD([sQuery(id+"F8.wireOp",EDGE,"E25.0.6.0")])]}),"instanceName":"34"});
            var Q279;
            Q279=makeQuery(id+"F10.opPattern","COPY",BODY,{"derivedFrom":makeQuery(id+"F9.opExtrude","SWEPT_BODY",BODY,{"disambiguationData":[OSD([sQuery(id+"F8.wireOp",EDGE,"E25.0.7.0")])]}),"instanceName":"34"});
            var Q280;
            Q280=makeQuery(id+"F10.opPattern","COPY",BODY,{"derivedFrom":makeQuery(id+"F9.opExtrude","SWEPT_BODY",BODY,{"disambiguationData":[OSD([sQuery(id+"F8.wireOp",EDGE,"E24")])]}),"instanceName":"35"});
            var Q281;
            Q281=makeQuery(id+"F10.opPattern","COPY",BODY,{"derivedFrom":makeQuery(id+"F9.opExtrude","SWEPT_BODY",BODY,{"disambiguationData":[OSD([sQuery(id+"F8.wireOp",EDGE,"E25.0.1.0")])]}),"instanceName":"35"});
            var Q282;
            Q282=makeQuery(id+"F10.opPattern","COPY",BODY,{"derivedFrom":makeQuery(id+"F9.opExtrude","SWEPT_BODY",BODY,{"disambiguationData":[OSD([sQuery(id+"F8.wireOp",EDGE,"E25.0.2.0")])]}),"instanceName":"35"});
            var Q283;
            Q283=makeQuery(id+"F10.opPattern","COPY",BODY,{"derivedFrom":makeQuery(id+"F9.opExtrude","SWEPT_BODY",BODY,{"disambiguationData":[OSD([sQuery(id+"F8.wireOp",EDGE,"E25.0.3.0")])]}),"instanceName":"35"});
            var Q284;
            Q284=makeQuery(id+"F10.opPattern","COPY",BODY,{"derivedFrom":makeQuery(id+"F9.opExtrude","SWEPT_BODY",BODY,{"disambiguationData":[OSD([sQuery(id+"F8.wireOp",EDGE,"E25.0.4.0")])]}),"instanceName":"35"});
            var Q285;
            Q285=makeQuery(id+"F10.opPattern","COPY",BODY,{"derivedFrom":makeQuery(id+"F9.opExtrude","SWEPT_BODY",BODY,{"disambiguationData":[OSD([sQuery(id+"F8.wireOp",EDGE,"E25.0.5.0")])]}),"instanceName":"35"});
            var Q286;
            Q286=makeQuery(id+"F10.opPattern","COPY",BODY,{"derivedFrom":makeQuery(id+"F9.opExtrude","SWEPT_BODY",BODY,{"disambiguationData":[OSD([sQuery(id+"F8.wireOp",EDGE,"E25.0.6.0")])]}),"instanceName":"35"});
            var Q287;
            Q287=makeQuery(id+"F10.opPattern","COPY",BODY,{"derivedFrom":makeQuery(id+"F9.opExtrude","SWEPT_BODY",BODY,{"disambiguationData":[OSD([sQuery(id+"F8.wireOp",EDGE,"E25.0.7.0")])]}),"instanceName":"35"});
            var Q288;
            Q288=makeQuery(id+"F10.opPattern","COPY",BODY,{"derivedFrom":makeQuery(id+"F9.opExtrude","SWEPT_BODY",BODY,{"disambiguationData":[OSD([sQuery(id+"F8.wireOp",EDGE,"E24")])]}),"instanceName":"36"});
            var Q289;
            Q289=makeQuery(id+"F10.opPattern","COPY",BODY,{"derivedFrom":makeQuery(id+"F9.opExtrude","SWEPT_BODY",BODY,{"disambiguationData":[OSD([sQuery(id+"F8.wireOp",EDGE,"E25.0.1.0")])]}),"instanceName":"36"});
            var Q290;
            Q290=makeQuery(id+"F10.opPattern","COPY",BODY,{"derivedFrom":makeQuery(id+"F9.opExtrude","SWEPT_BODY",BODY,{"disambiguationData":[OSD([sQuery(id+"F8.wireOp",EDGE,"E25.0.2.0")])]}),"instanceName":"36"});
            var Q291;
            Q291=makeQuery(id+"F10.opPattern","COPY",BODY,{"derivedFrom":makeQuery(id+"F9.opExtrude","SWEPT_BODY",BODY,{"disambiguationData":[OSD([sQuery(id+"F8.wireOp",EDGE,"E25.0.3.0")])]}),"instanceName":"36"});
            var Q292;
            Q292=makeQuery(id+"F10.opPattern","COPY",BODY,{"derivedFrom":makeQuery(id+"F9.opExtrude","SWEPT_BODY",BODY,{"disambiguationData":[OSD([sQuery(id+"F8.wireOp",EDGE,"E25.0.4.0")])]}),"instanceName":"36"});
            var Q293;
            Q293=makeQuery(id+"F10.opPattern","COPY",BODY,{"derivedFrom":makeQuery(id+"F9.opExtrude","SWEPT_BODY",BODY,{"disambiguationData":[OSD([sQuery(id+"F8.wireOp",EDGE,"E25.0.5.0")])]}),"instanceName":"36"});
            var Q294;
            Q294=makeQuery(id+"F10.opPattern","COPY",BODY,{"derivedFrom":makeQuery(id+"F9.opExtrude","SWEPT_BODY",BODY,{"disambiguationData":[OSD([sQuery(id+"F8.wireOp",EDGE,"E25.0.6.0")])]}),"instanceName":"36"});
            var Q295;
            Q295=makeQuery(id+"F10.opPattern","COPY",BODY,{"derivedFrom":makeQuery(id+"F9.opExtrude","SWEPT_BODY",BODY,{"disambiguationData":[OSD([sQuery(id+"F8.wireOp",EDGE,"E25.0.7.0")])]}),"instanceName":"36"});
            var Q296;
            Q296=makeQuery(id+"F10.opPattern","COPY",BODY,{"derivedFrom":makeQuery(id+"F9.opExtrude","SWEPT_BODY",BODY,{"disambiguationData":[OSD([sQuery(id+"F8.wireOp",EDGE,"E24")])]}),"instanceName":"37"});
            var Q297;
            Q297=makeQuery(id+"F10.opPattern","COPY",BODY,{"derivedFrom":makeQuery(id+"F9.opExtrude","SWEPT_BODY",BODY,{"disambiguationData":[OSD([sQuery(id+"F8.wireOp",EDGE,"E25.0.1.0")])]}),"instanceName":"37"});
            var Q298;
            Q298=makeQuery(id+"F10.opPattern","COPY",BODY,{"derivedFrom":makeQuery(id+"F9.opExtrude","SWEPT_BODY",BODY,{"disambiguationData":[OSD([sQuery(id+"F8.wireOp",EDGE,"E25.0.2.0")])]}),"instanceName":"37"});
            var Q299;
            Q299=makeQuery(id+"F10.opPattern","COPY",BODY,{"derivedFrom":makeQuery(id+"F9.opExtrude","SWEPT_BODY",BODY,{"disambiguationData":[OSD([sQuery(id+"F8.wireOp",EDGE,"E25.0.3.0")])]}),"instanceName":"37"});
            var Q300;
            Q300=makeQuery(id+"F10.opPattern","COPY",BODY,{"derivedFrom":makeQuery(id+"F9.opExtrude","SWEPT_BODY",BODY,{"disambiguationData":[OSD([sQuery(id+"F8.wireOp",EDGE,"E25.0.4.0")])]}),"instanceName":"37"});
            var Q301;
            Q301=makeQuery(id+"F10.opPattern","COPY",BODY,{"derivedFrom":makeQuery(id+"F9.opExtrude","SWEPT_BODY",BODY,{"disambiguationData":[OSD([sQuery(id+"F8.wireOp",EDGE,"E25.0.5.0")])]}),"instanceName":"37"});
            var Q302;
            Q302=makeQuery(id+"F10.opPattern","COPY",BODY,{"derivedFrom":makeQuery(id+"F9.opExtrude","SWEPT_BODY",BODY,{"disambiguationData":[OSD([sQuery(id+"F8.wireOp",EDGE,"E25.0.6.0")])]}),"instanceName":"37"});
            var Q303;
            Q303=makeQuery(id+"F10.opPattern","COPY",BODY,{"derivedFrom":makeQuery(id+"F9.opExtrude","SWEPT_BODY",BODY,{"disambiguationData":[OSD([sQuery(id+"F8.wireOp",EDGE,"E25.0.7.0")])]}),"instanceName":"37"});
            var Q304;
            Q304=makeQuery(id+"F10.opPattern","COPY",BODY,{"derivedFrom":makeQuery(id+"F9.opExtrude","SWEPT_BODY",BODY,{"disambiguationData":[OSD([sQuery(id+"F8.wireOp",EDGE,"E24")])]}),"instanceName":"38"});
            var Q305;
            Q305=makeQuery(id+"F10.opPattern","COPY",BODY,{"derivedFrom":makeQuery(id+"F9.opExtrude","SWEPT_BODY",BODY,{"disambiguationData":[OSD([sQuery(id+"F8.wireOp",EDGE,"E25.0.1.0")])]}),"instanceName":"38"});
            var Q306;
            Q306=makeQuery(id+"F10.opPattern","COPY",BODY,{"derivedFrom":makeQuery(id+"F9.opExtrude","SWEPT_BODY",BODY,{"disambiguationData":[OSD([sQuery(id+"F8.wireOp",EDGE,"E25.0.2.0")])]}),"instanceName":"38"});
            var Q307;
            Q307=makeQuery(id+"F10.opPattern","COPY",BODY,{"derivedFrom":makeQuery(id+"F9.opExtrude","SWEPT_BODY",BODY,{"disambiguationData":[OSD([sQuery(id+"F8.wireOp",EDGE,"E25.0.3.0")])]}),"instanceName":"38"});
            var Q308;
            Q308=makeQuery(id+"F10.opPattern","COPY",BODY,{"derivedFrom":makeQuery(id+"F9.opExtrude","SWEPT_BODY",BODY,{"disambiguationData":[OSD([sQuery(id+"F8.wireOp",EDGE,"E25.0.4.0")])]}),"instanceName":"38"});
            var Q309;
            Q309=makeQuery(id+"F10.opPattern","COPY",BODY,{"derivedFrom":makeQuery(id+"F9.opExtrude","SWEPT_BODY",BODY,{"disambiguationData":[OSD([sQuery(id+"F8.wireOp",EDGE,"E25.0.5.0")])]}),"instanceName":"38"});
            var Q310;
            Q310=makeQuery(id+"F10.opPattern","COPY",BODY,{"derivedFrom":makeQuery(id+"F9.opExtrude","SWEPT_BODY",BODY,{"disambiguationData":[OSD([sQuery(id+"F8.wireOp",EDGE,"E25.0.6.0")])]}),"instanceName":"38"});
            var Q311;
            Q311=makeQuery(id+"F10.opPattern","COPY",BODY,{"derivedFrom":makeQuery(id+"F9.opExtrude","SWEPT_BODY",BODY,{"disambiguationData":[OSD([sQuery(id+"F8.wireOp",EDGE,"E25.0.7.0")])]}),"instanceName":"38"});
            var Q312;
            Q312=makeQuery(id+"F10.opPattern","COPY",BODY,{"derivedFrom":makeQuery(id+"F9.opExtrude","SWEPT_BODY",BODY,{"disambiguationData":[OSD([sQuery(id+"F8.wireOp",EDGE,"E24")])]}),"instanceName":"39"});
            var Q313;
            Q313=makeQuery(id+"F10.opPattern","COPY",BODY,{"derivedFrom":makeQuery(id+"F9.opExtrude","SWEPT_BODY",BODY,{"disambiguationData":[OSD([sQuery(id+"F8.wireOp",EDGE,"E25.0.1.0")])]}),"instanceName":"39"});
            var Q314;
            Q314=makeQuery(id+"F10.opPattern","COPY",BODY,{"derivedFrom":makeQuery(id+"F9.opExtrude","SWEPT_BODY",BODY,{"disambiguationData":[OSD([sQuery(id+"F8.wireOp",EDGE,"E25.0.2.0")])]}),"instanceName":"39"});
            var Q315;
            Q315=makeQuery(id+"F10.opPattern","COPY",BODY,{"derivedFrom":makeQuery(id+"F9.opExtrude","SWEPT_BODY",BODY,{"disambiguationData":[OSD([sQuery(id+"F8.wireOp",EDGE,"E25.0.3.0")])]}),"instanceName":"39"});
            var Q316;
            Q316=makeQuery(id+"F10.opPattern","COPY",BODY,{"derivedFrom":makeQuery(id+"F9.opExtrude","SWEPT_BODY",BODY,{"disambiguationData":[OSD([sQuery(id+"F8.wireOp",EDGE,"E25.0.4.0")])]}),"instanceName":"39"});
            var Q317;
            Q317=makeQuery(id+"F10.opPattern","COPY",BODY,{"derivedFrom":makeQuery(id+"F9.opExtrude","SWEPT_BODY",BODY,{"disambiguationData":[OSD([sQuery(id+"F8.wireOp",EDGE,"E25.0.5.0")])]}),"instanceName":"39"});
            var Q318;
            Q318=makeQuery(id+"F10.opPattern","COPY",BODY,{"derivedFrom":makeQuery(id+"F9.opExtrude","SWEPT_BODY",BODY,{"disambiguationData":[OSD([sQuery(id+"F8.wireOp",EDGE,"E25.0.6.0")])]}),"instanceName":"39"});
            var Q319;
            Q319=makeQuery(id+"F10.opPattern","COPY",BODY,{"derivedFrom":makeQuery(id+"F9.opExtrude","SWEPT_BODY",BODY,{"disambiguationData":[OSD([sQuery(id+"F8.wireOp",EDGE,"E25.0.7.0")])]}),"instanceName":"39"});
            var Q320;
            Q320=makeQuery(id+"F10.opPattern","COPY",BODY,{"derivedFrom":makeQuery(id+"F9.opExtrude","SWEPT_BODY",BODY,{"disambiguationData":[OSD([sQuery(id+"F8.wireOp",EDGE,"E24")])]}),"instanceName":"40"});
            var Q321;
            Q321=makeQuery(id+"F10.opPattern","COPY",BODY,{"derivedFrom":makeQuery(id+"F9.opExtrude","SWEPT_BODY",BODY,{"disambiguationData":[OSD([sQuery(id+"F8.wireOp",EDGE,"E25.0.1.0")])]}),"instanceName":"40"});
            var Q322;
            Q322=makeQuery(id+"F10.opPattern","COPY",BODY,{"derivedFrom":makeQuery(id+"F9.opExtrude","SWEPT_BODY",BODY,{"disambiguationData":[OSD([sQuery(id+"F8.wireOp",EDGE,"E25.0.2.0")])]}),"instanceName":"40"});
            var Q323;
            Q323=makeQuery(id+"F10.opPattern","COPY",BODY,{"derivedFrom":makeQuery(id+"F9.opExtrude","SWEPT_BODY",BODY,{"disambiguationData":[OSD([sQuery(id+"F8.wireOp",EDGE,"E25.0.3.0")])]}),"instanceName":"40"});
            var Q324;
            Q324=makeQuery(id+"F10.opPattern","COPY",BODY,{"derivedFrom":makeQuery(id+"F9.opExtrude","SWEPT_BODY",BODY,{"disambiguationData":[OSD([sQuery(id+"F8.wireOp",EDGE,"E25.0.4.0")])]}),"instanceName":"40"});
            var Q325;
            Q325=makeQuery(id+"F10.opPattern","COPY",BODY,{"derivedFrom":makeQuery(id+"F9.opExtrude","SWEPT_BODY",BODY,{"disambiguationData":[OSD([sQuery(id+"F8.wireOp",EDGE,"E25.0.5.0")])]}),"instanceName":"40"});
            var Q326;
            Q326=makeQuery(id+"F10.opPattern","COPY",BODY,{"derivedFrom":makeQuery(id+"F9.opExtrude","SWEPT_BODY",BODY,{"disambiguationData":[OSD([sQuery(id+"F8.wireOp",EDGE,"E25.0.6.0")])]}),"instanceName":"40"});
            var Q327;
            Q327=makeQuery(id+"F10.opPattern","COPY",BODY,{"derivedFrom":makeQuery(id+"F9.opExtrude","SWEPT_BODY",BODY,{"disambiguationData":[OSD([sQuery(id+"F8.wireOp",EDGE,"E25.0.7.0")])]}),"instanceName":"40"});
            var Q328;
            Q328=makeQuery(id+"F10.opPattern","COPY",BODY,{"derivedFrom":makeQuery(id+"F9.opExtrude","SWEPT_BODY",BODY,{"disambiguationData":[OSD([sQuery(id+"F8.wireOp",EDGE,"E24")])]}),"instanceName":"41"});
            var Q329;
            Q329=makeQuery(id+"F10.opPattern","COPY",BODY,{"derivedFrom":makeQuery(id+"F9.opExtrude","SWEPT_BODY",BODY,{"disambiguationData":[OSD([sQuery(id+"F8.wireOp",EDGE,"E25.0.1.0")])]}),"instanceName":"41"});
            var Q330;
            Q330=makeQuery(id+"F10.opPattern","COPY",BODY,{"derivedFrom":makeQuery(id+"F9.opExtrude","SWEPT_BODY",BODY,{"disambiguationData":[OSD([sQuery(id+"F8.wireOp",EDGE,"E25.0.2.0")])]}),"instanceName":"41"});
            var Q331;
            Q331=makeQuery(id+"F10.opPattern","COPY",BODY,{"derivedFrom":makeQuery(id+"F9.opExtrude","SWEPT_BODY",BODY,{"disambiguationData":[OSD([sQuery(id+"F8.wireOp",EDGE,"E25.0.3.0")])]}),"instanceName":"41"});
            var Q332;
            Q332=makeQuery(id+"F10.opPattern","COPY",BODY,{"derivedFrom":makeQuery(id+"F9.opExtrude","SWEPT_BODY",BODY,{"disambiguationData":[OSD([sQuery(id+"F8.wireOp",EDGE,"E25.0.4.0")])]}),"instanceName":"41"});
            var Q333;
            Q333=makeQuery(id+"F10.opPattern","COPY",BODY,{"derivedFrom":makeQuery(id+"F9.opExtrude","SWEPT_BODY",BODY,{"disambiguationData":[OSD([sQuery(id+"F8.wireOp",EDGE,"E25.0.5.0")])]}),"instanceName":"41"});
            var Q334;
            Q334=makeQuery(id+"F10.opPattern","COPY",BODY,{"derivedFrom":makeQuery(id+"F9.opExtrude","SWEPT_BODY",BODY,{"disambiguationData":[OSD([sQuery(id+"F8.wireOp",EDGE,"E25.0.6.0")])]}),"instanceName":"41"});
            var Q335;
            Q335=makeQuery(id+"F10.opPattern","COPY",BODY,{"derivedFrom":makeQuery(id+"F9.opExtrude","SWEPT_BODY",BODY,{"disambiguationData":[OSD([sQuery(id+"F8.wireOp",EDGE,"E25.0.7.0")])]}),"instanceName":"41"});
            var Q336;
            Q336=makeQuery(id+"F10.opPattern","COPY",BODY,{"derivedFrom":makeQuery(id+"F9.opExtrude","SWEPT_BODY",BODY,{"disambiguationData":[OSD([sQuery(id+"F8.wireOp",EDGE,"E24")])]}),"instanceName":"42"});
            var Q337;
            Q337=makeQuery(id+"F10.opPattern","COPY",BODY,{"derivedFrom":makeQuery(id+"F9.opExtrude","SWEPT_BODY",BODY,{"disambiguationData":[OSD([sQuery(id+"F8.wireOp",EDGE,"E25.0.1.0")])]}),"instanceName":"42"});
            var Q338;
            Q338=makeQuery(id+"F10.opPattern","COPY",BODY,{"derivedFrom":makeQuery(id+"F9.opExtrude","SWEPT_BODY",BODY,{"disambiguationData":[OSD([sQuery(id+"F8.wireOp",EDGE,"E25.0.2.0")])]}),"instanceName":"42"});
            var Q339;
            Q339=makeQuery(id+"F10.opPattern","COPY",BODY,{"derivedFrom":makeQuery(id+"F9.opExtrude","SWEPT_BODY",BODY,{"disambiguationData":[OSD([sQuery(id+"F8.wireOp",EDGE,"E25.0.3.0")])]}),"instanceName":"42"});
            var Q340;
            Q340=makeQuery(id+"F10.opPattern","COPY",BODY,{"derivedFrom":makeQuery(id+"F9.opExtrude","SWEPT_BODY",BODY,{"disambiguationData":[OSD([sQuery(id+"F8.wireOp",EDGE,"E25.0.4.0")])]}),"instanceName":"42"});
            var Q341;
            Q341=makeQuery(id+"F10.opPattern","COPY",BODY,{"derivedFrom":makeQuery(id+"F9.opExtrude","SWEPT_BODY",BODY,{"disambiguationData":[OSD([sQuery(id+"F8.wireOp",EDGE,"E25.0.5.0")])]}),"instanceName":"42"});
            var Q342;
            Q342=makeQuery(id+"F10.opPattern","COPY",BODY,{"derivedFrom":makeQuery(id+"F9.opExtrude","SWEPT_BODY",BODY,{"disambiguationData":[OSD([sQuery(id+"F8.wireOp",EDGE,"E25.0.6.0")])]}),"instanceName":"42"});
            var Q343;
            Q343=makeQuery(id+"F10.opPattern","COPY",BODY,{"derivedFrom":makeQuery(id+"F9.opExtrude","SWEPT_BODY",BODY,{"disambiguationData":[OSD([sQuery(id+"F8.wireOp",EDGE,"E25.0.7.0")])]}),"instanceName":"42"});
            var Q344;
            Q344=makeQuery(id+"F10.opPattern","COPY",BODY,{"derivedFrom":makeQuery(id+"F9.opExtrude","SWEPT_BODY",BODY,{"disambiguationData":[OSD([sQuery(id+"F8.wireOp",EDGE,"E24")])]}),"instanceName":"43"});
            var Q345;
            Q345=makeQuery(id+"F10.opPattern","COPY",BODY,{"derivedFrom":makeQuery(id+"F9.opExtrude","SWEPT_BODY",BODY,{"disambiguationData":[OSD([sQuery(id+"F8.wireOp",EDGE,"E25.0.1.0")])]}),"instanceName":"43"});
            var Q346;
            Q346=makeQuery(id+"F10.opPattern","COPY",BODY,{"derivedFrom":makeQuery(id+"F9.opExtrude","SWEPT_BODY",BODY,{"disambiguationData":[OSD([sQuery(id+"F8.wireOp",EDGE,"E25.0.2.0")])]}),"instanceName":"43"});
            var Q347;
            Q347=makeQuery(id+"F10.opPattern","COPY",BODY,{"derivedFrom":makeQuery(id+"F9.opExtrude","SWEPT_BODY",BODY,{"disambiguationData":[OSD([sQuery(id+"F8.wireOp",EDGE,"E25.0.3.0")])]}),"instanceName":"43"});
            var Q348;
            Q348=makeQuery(id+"F10.opPattern","COPY",BODY,{"derivedFrom":makeQuery(id+"F9.opExtrude","SWEPT_BODY",BODY,{"disambiguationData":[OSD([sQuery(id+"F8.wireOp",EDGE,"E25.0.4.0")])]}),"instanceName":"43"});
            var Q349;
            Q349=makeQuery(id+"F10.opPattern","COPY",BODY,{"derivedFrom":makeQuery(id+"F9.opExtrude","SWEPT_BODY",BODY,{"disambiguationData":[OSD([sQuery(id+"F8.wireOp",EDGE,"E25.0.5.0")])]}),"instanceName":"43"});
            var Q350;
            Q350=makeQuery(id+"F10.opPattern","COPY",BODY,{"derivedFrom":makeQuery(id+"F9.opExtrude","SWEPT_BODY",BODY,{"disambiguationData":[OSD([sQuery(id+"F8.wireOp",EDGE,"E25.0.6.0")])]}),"instanceName":"43"});
            var Q351;
            Q351=makeQuery(id+"F10.opPattern","COPY",BODY,{"derivedFrom":makeQuery(id+"F9.opExtrude","SWEPT_BODY",BODY,{"disambiguationData":[OSD([sQuery(id+"F8.wireOp",EDGE,"E25.0.7.0")])]}),"instanceName":"43"});
            var Q352;
            Q352=makeQuery(id+"F10.opPattern","COPY",BODY,{"derivedFrom":makeQuery(id+"F9.opExtrude","SWEPT_BODY",BODY,{"disambiguationData":[OSD([sQuery(id+"F8.wireOp",EDGE,"E24")])]}),"instanceName":"44"});
            var Q353;
            Q353=makeQuery(id+"F10.opPattern","COPY",BODY,{"derivedFrom":makeQuery(id+"F9.opExtrude","SWEPT_BODY",BODY,{"disambiguationData":[OSD([sQuery(id+"F8.wireOp",EDGE,"E25.0.1.0")])]}),"instanceName":"44"});
            var Q354;
            Q354=makeQuery(id+"F10.opPattern","COPY",BODY,{"derivedFrom":makeQuery(id+"F9.opExtrude","SWEPT_BODY",BODY,{"disambiguationData":[OSD([sQuery(id+"F8.wireOp",EDGE,"E25.0.2.0")])]}),"instanceName":"44"});
            var Q355;
            Q355=makeQuery(id+"F10.opPattern","COPY",BODY,{"derivedFrom":makeQuery(id+"F9.opExtrude","SWEPT_BODY",BODY,{"disambiguationData":[OSD([sQuery(id+"F8.wireOp",EDGE,"E25.0.3.0")])]}),"instanceName":"44"});
            var Q356;
            Q356=makeQuery(id+"F10.opPattern","COPY",BODY,{"derivedFrom":makeQuery(id+"F9.opExtrude","SWEPT_BODY",BODY,{"disambiguationData":[OSD([sQuery(id+"F8.wireOp",EDGE,"E25.0.4.0")])]}),"instanceName":"44"});
            var Q357;
            Q357=makeQuery(id+"F10.opPattern","COPY",BODY,{"derivedFrom":makeQuery(id+"F9.opExtrude","SWEPT_BODY",BODY,{"disambiguationData":[OSD([sQuery(id+"F8.wireOp",EDGE,"E25.0.5.0")])]}),"instanceName":"44"});
            var Q358;
            Q358=makeQuery(id+"F10.opPattern","COPY",BODY,{"derivedFrom":makeQuery(id+"F9.opExtrude","SWEPT_BODY",BODY,{"disambiguationData":[OSD([sQuery(id+"F8.wireOp",EDGE,"E25.0.6.0")])]}),"instanceName":"44"});
            var Q359;
            Q359=makeQuery(id+"F10.opPattern","COPY",BODY,{"derivedFrom":makeQuery(id+"F9.opExtrude","SWEPT_BODY",BODY,{"disambiguationData":[OSD([sQuery(id+"F8.wireOp",EDGE,"E25.0.7.0")])]}),"instanceName":"44"});
            var Q360;
            Q360=makeQuery(id+"F10.opPattern","COPY",BODY,{"derivedFrom":makeQuery(id+"F9.opExtrude","SWEPT_BODY",BODY,{"disambiguationData":[OSD([sQuery(id+"F8.wireOp",EDGE,"E24")])]}),"instanceName":"45"});
            var Q361;
            Q361=makeQuery(id+"F10.opPattern","COPY",BODY,{"derivedFrom":makeQuery(id+"F9.opExtrude","SWEPT_BODY",BODY,{"disambiguationData":[OSD([sQuery(id+"F8.wireOp",EDGE,"E25.0.1.0")])]}),"instanceName":"45"});
            var Q362;
            Q362=makeQuery(id+"F10.opPattern","COPY",BODY,{"derivedFrom":makeQuery(id+"F9.opExtrude","SWEPT_BODY",BODY,{"disambiguationData":[OSD([sQuery(id+"F8.wireOp",EDGE,"E25.0.2.0")])]}),"instanceName":"45"});
            var Q363;
            Q363=makeQuery(id+"F10.opPattern","COPY",BODY,{"derivedFrom":makeQuery(id+"F9.opExtrude","SWEPT_BODY",BODY,{"disambiguationData":[OSD([sQuery(id+"F8.wireOp",EDGE,"E25.0.3.0")])]}),"instanceName":"45"});
            var Q364;
            Q364=makeQuery(id+"F10.opPattern","COPY",BODY,{"derivedFrom":makeQuery(id+"F9.opExtrude","SWEPT_BODY",BODY,{"disambiguationData":[OSD([sQuery(id+"F8.wireOp",EDGE,"E25.0.4.0")])]}),"instanceName":"45"});
            var Q365;
            Q365=makeQuery(id+"F10.opPattern","COPY",BODY,{"derivedFrom":makeQuery(id+"F9.opExtrude","SWEPT_BODY",BODY,{"disambiguationData":[OSD([sQuery(id+"F8.wireOp",EDGE,"E25.0.5.0")])]}),"instanceName":"45"});
            var Q366;
            Q366=makeQuery(id+"F10.opPattern","COPY",BODY,{"derivedFrom":makeQuery(id+"F9.opExtrude","SWEPT_BODY",BODY,{"disambiguationData":[OSD([sQuery(id+"F8.wireOp",EDGE,"E25.0.6.0")])]}),"instanceName":"45"});
            var Q367;
            Q367=makeQuery(id+"F10.opPattern","COPY",BODY,{"derivedFrom":makeQuery(id+"F9.opExtrude","SWEPT_BODY",BODY,{"disambiguationData":[OSD([sQuery(id+"F8.wireOp",EDGE,"E25.0.7.0")])]}),"instanceName":"45"});
            var Q368;
            Q368=makeQuery(id+"F10.opPattern","COPY",BODY,{"derivedFrom":makeQuery(id+"F9.opExtrude","SWEPT_BODY",BODY,{"disambiguationData":[OSD([sQuery(id+"F8.wireOp",EDGE,"E24")])]}),"instanceName":"46"});
            var Q369;
            Q369=makeQuery(id+"F10.opPattern","COPY",BODY,{"derivedFrom":makeQuery(id+"F9.opExtrude","SWEPT_BODY",BODY,{"disambiguationData":[OSD([sQuery(id+"F8.wireOp",EDGE,"E25.0.1.0")])]}),"instanceName":"46"});
            var Q370;
            Q370=makeQuery(id+"F10.opPattern","COPY",BODY,{"derivedFrom":makeQuery(id+"F9.opExtrude","SWEPT_BODY",BODY,{"disambiguationData":[OSD([sQuery(id+"F8.wireOp",EDGE,"E25.0.2.0")])]}),"instanceName":"46"});
            var Q371;
            Q371=makeQuery(id+"F10.opPattern","COPY",BODY,{"derivedFrom":makeQuery(id+"F9.opExtrude","SWEPT_BODY",BODY,{"disambiguationData":[OSD([sQuery(id+"F8.wireOp",EDGE,"E25.0.3.0")])]}),"instanceName":"46"});
            var Q372;
            Q372=makeQuery(id+"F10.opPattern","COPY",BODY,{"derivedFrom":makeQuery(id+"F9.opExtrude","SWEPT_BODY",BODY,{"disambiguationData":[OSD([sQuery(id+"F8.wireOp",EDGE,"E25.0.4.0")])]}),"instanceName":"46"});
            var Q373;
            Q373=makeQuery(id+"F10.opPattern","COPY",BODY,{"derivedFrom":makeQuery(id+"F9.opExtrude","SWEPT_BODY",BODY,{"disambiguationData":[OSD([sQuery(id+"F8.wireOp",EDGE,"E25.0.5.0")])]}),"instanceName":"46"});
            var Q374;
            Q374=makeQuery(id+"F10.opPattern","COPY",BODY,{"derivedFrom":makeQuery(id+"F9.opExtrude","SWEPT_BODY",BODY,{"disambiguationData":[OSD([sQuery(id+"F8.wireOp",EDGE,"E25.0.6.0")])]}),"instanceName":"46"});
            var Q375;
            Q375=makeQuery(id+"F10.opPattern","COPY",BODY,{"derivedFrom":makeQuery(id+"F9.opExtrude","SWEPT_BODY",BODY,{"disambiguationData":[OSD([sQuery(id+"F8.wireOp",EDGE,"E25.0.7.0")])]}),"instanceName":"46"});
            var Q376;
            Q376=makeQuery(id+"F10.opPattern","COPY",BODY,{"derivedFrom":makeQuery(id+"F9.opExtrude","SWEPT_BODY",BODY,{"disambiguationData":[OSD([sQuery(id+"F8.wireOp",EDGE,"E24")])]}),"instanceName":"47"});
            var Q377;
            Q377=makeQuery(id+"F10.opPattern","COPY",BODY,{"derivedFrom":makeQuery(id+"F9.opExtrude","SWEPT_BODY",BODY,{"disambiguationData":[OSD([sQuery(id+"F8.wireOp",EDGE,"E25.0.1.0")])]}),"instanceName":"47"});
            var Q378;
            Q378=makeQuery(id+"F10.opPattern","COPY",BODY,{"derivedFrom":makeQuery(id+"F9.opExtrude","SWEPT_BODY",BODY,{"disambiguationData":[OSD([sQuery(id+"F8.wireOp",EDGE,"E25.0.2.0")])]}),"instanceName":"47"});
            var Q379;
            Q379=makeQuery(id+"F10.opPattern","COPY",BODY,{"derivedFrom":makeQuery(id+"F9.opExtrude","SWEPT_BODY",BODY,{"disambiguationData":[OSD([sQuery(id+"F8.wireOp",EDGE,"E25.0.3.0")])]}),"instanceName":"47"});
            var Q380;
            Q380=makeQuery(id+"F10.opPattern","COPY",BODY,{"derivedFrom":makeQuery(id+"F9.opExtrude","SWEPT_BODY",BODY,{"disambiguationData":[OSD([sQuery(id+"F8.wireOp",EDGE,"E25.0.4.0")])]}),"instanceName":"47"});
            var Q381;
            Q381=makeQuery(id+"F10.opPattern","COPY",BODY,{"derivedFrom":makeQuery(id+"F9.opExtrude","SWEPT_BODY",BODY,{"disambiguationData":[OSD([sQuery(id+"F8.wireOp",EDGE,"E25.0.5.0")])]}),"instanceName":"47"});
            var Q382;
            Q382=makeQuery(id+"F10.opPattern","COPY",BODY,{"derivedFrom":makeQuery(id+"F9.opExtrude","SWEPT_BODY",BODY,{"disambiguationData":[OSD([sQuery(id+"F8.wireOp",EDGE,"E25.0.6.0")])]}),"instanceName":"47"});
            var Q383;
            Q383=makeQuery(id+"F10.opPattern","COPY",BODY,{"derivedFrom":makeQuery(id+"F9.opExtrude","SWEPT_BODY",BODY,{"disambiguationData":[OSD([sQuery(id+"F8.wireOp",EDGE,"E25.0.7.0")])]}),"instanceName":"47"});
            var Q384;
            Q384=makeQuery(id+"F10.opPattern","COPY",BODY,{"derivedFrom":makeQuery(id+"F9.opExtrude","SWEPT_BODY",BODY,{"disambiguationData":[OSD([sQuery(id+"F8.wireOp",EDGE,"E24")])]}),"instanceName":"48"});
            var Q385;
            Q385=makeQuery(id+"F10.opPattern","COPY",BODY,{"derivedFrom":makeQuery(id+"F9.opExtrude","SWEPT_BODY",BODY,{"disambiguationData":[OSD([sQuery(id+"F8.wireOp",EDGE,"E25.0.1.0")])]}),"instanceName":"48"});
            var Q386;
            Q386=makeQuery(id+"F10.opPattern","COPY",BODY,{"derivedFrom":makeQuery(id+"F9.opExtrude","SWEPT_BODY",BODY,{"disambiguationData":[OSD([sQuery(id+"F8.wireOp",EDGE,"E25.0.2.0")])]}),"instanceName":"48"});
            var Q387;
            Q387=makeQuery(id+"F10.opPattern","COPY",BODY,{"derivedFrom":makeQuery(id+"F9.opExtrude","SWEPT_BODY",BODY,{"disambiguationData":[OSD([sQuery(id+"F8.wireOp",EDGE,"E25.0.3.0")])]}),"instanceName":"48"});
            var Q388;
            Q388=makeQuery(id+"F10.opPattern","COPY",BODY,{"derivedFrom":makeQuery(id+"F9.opExtrude","SWEPT_BODY",BODY,{"disambiguationData":[OSD([sQuery(id+"F8.wireOp",EDGE,"E25.0.4.0")])]}),"instanceName":"48"});
            var Q389;
            Q389=makeQuery(id+"F10.opPattern","COPY",BODY,{"derivedFrom":makeQuery(id+"F9.opExtrude","SWEPT_BODY",BODY,{"disambiguationData":[OSD([sQuery(id+"F8.wireOp",EDGE,"E25.0.5.0")])]}),"instanceName":"48"});
            var Q390;
            Q390=makeQuery(id+"F10.opPattern","COPY",BODY,{"derivedFrom":makeQuery(id+"F9.opExtrude","SWEPT_BODY",BODY,{"disambiguationData":[OSD([sQuery(id+"F8.wireOp",EDGE,"E25.0.6.0")])]}),"instanceName":"48"});
            var Q391;
            Q391=makeQuery(id+"F10.opPattern","COPY",BODY,{"derivedFrom":makeQuery(id+"F9.opExtrude","SWEPT_BODY",BODY,{"disambiguationData":[OSD([sQuery(id+"F8.wireOp",EDGE,"E25.0.7.0")])]}),"instanceName":"48"});
            var Q392;
            Q392=makeQuery(id+"F10.opPattern","COPY",BODY,{"derivedFrom":makeQuery(id+"F9.opExtrude","SWEPT_BODY",BODY,{"disambiguationData":[OSD([sQuery(id+"F8.wireOp",EDGE,"E24")])]}),"instanceName":"49"});
            var Q393;
            Q393=makeQuery(id+"F10.opPattern","COPY",BODY,{"derivedFrom":makeQuery(id+"F9.opExtrude","SWEPT_BODY",BODY,{"disambiguationData":[OSD([sQuery(id+"F8.wireOp",EDGE,"E25.0.1.0")])]}),"instanceName":"49"});
            var Q394;
            Q394=makeQuery(id+"F10.opPattern","COPY",BODY,{"derivedFrom":makeQuery(id+"F9.opExtrude","SWEPT_BODY",BODY,{"disambiguationData":[OSD([sQuery(id+"F8.wireOp",EDGE,"E25.0.2.0")])]}),"instanceName":"49"});
            var Q395;
            Q395=makeQuery(id+"F10.opPattern","COPY",BODY,{"derivedFrom":makeQuery(id+"F9.opExtrude","SWEPT_BODY",BODY,{"disambiguationData":[OSD([sQuery(id+"F8.wireOp",EDGE,"E25.0.3.0")])]}),"instanceName":"49"});
            var Q396;
            Q396=makeQuery(id+"F10.opPattern","COPY",BODY,{"derivedFrom":makeQuery(id+"F9.opExtrude","SWEPT_BODY",BODY,{"disambiguationData":[OSD([sQuery(id+"F8.wireOp",EDGE,"E25.0.4.0")])]}),"instanceName":"49"});
            var Q397;
            Q397=makeQuery(id+"F10.opPattern","COPY",BODY,{"derivedFrom":makeQuery(id+"F9.opExtrude","SWEPT_BODY",BODY,{"disambiguationData":[OSD([sQuery(id+"F8.wireOp",EDGE,"E25.0.5.0")])]}),"instanceName":"49"});
            var Q398;
            Q398=makeQuery(id+"F10.opPattern","COPY",BODY,{"derivedFrom":makeQuery(id+"F9.opExtrude","SWEPT_BODY",BODY,{"disambiguationData":[OSD([sQuery(id+"F8.wireOp",EDGE,"E25.0.6.0")])]}),"instanceName":"49"});
            var Q399;
            Q399=makeQuery(id+"F10.opPattern","COPY",BODY,{"derivedFrom":makeQuery(id+"F9.opExtrude","SWEPT_BODY",BODY,{"disambiguationData":[OSD([sQuery(id+"F8.wireOp",EDGE,"E25.0.7.0")])]}),"instanceName":"49"});
            var Q400;
            Q400=makeQuery(id+"F1.opRevolve","SWEPT_BODY",BODY,{"disambiguationData":[OSD([sQuery(id+"F0.wireOp",EDGE,"E0"),sQuery(id+"F0.wireOp",EDGE,"E1"),sQuery(id+"F0.wireOp",EDGE,"E2"),sQuery(id+"F0.wireOp",EDGE,"E3"),sQuery(id+"F0.wireOp",EDGE,"E4"),sQuery(id+"F0.wireOp",EDGE,"E6"),sQuery(id+"F0.wireOp",EDGE,"E8"),sQuery(id+"F0.wireOp",EDGE,"E9"),sQuery(id+"F0.wireOp",EDGE,"E10"),sQuery(id+"F0.wireOp",EDGE,"E12"),sQuery(id+"F0.wireOp",EDGE,"E13"),sQuery(id+"F0.wireOp",EDGE,"E14")])]});
            booleanBodies(context, id + "F11", {"operationType" : BooleanOperationType.SUBTRACTION, "tools" : qUnion([Q0, Q1, Q2, Q3, Q4, Q5, Q6, Q7, Q8, Q9, Q10, Q11, Q12, Q13, Q14, Q15, Q16, Q17, Q18, Q19, Q20, Q21, Q22, Q23, Q24, Q25, Q26, Q27, Q28, Q29, Q30, Q31, Q32, Q33, Q34, Q35, Q36, Q37, Q38, Q39, Q40, Q41, Q42, Q43, Q44, Q45, Q46, Q47, Q48, Q49, Q50, Q51, Q52, Q53, Q54, Q55, Q56, Q57, Q58, Q59, Q60, Q61, Q62, Q63, Q64, Q65, Q66, Q67, Q68, Q69, Q70, Q71, Q72, Q73, Q74, Q75, Q76, Q77, Q78, Q79, Q80, Q81, Q82, Q83, Q84, Q85, Q86, Q87, Q88, Q89, Q90, Q91, Q92, Q93, Q94, Q95, Q96, Q97, Q98, Q99, Q100, Q101, Q102, Q103, Q104, Q105, Q106, Q107, Q108, Q109, Q110, Q111, Q112, Q113, Q114, Q115, Q116, Q117, Q118, Q119, Q120, Q121, Q122, Q123, Q124, Q125, Q126, Q127, Q128, Q129, Q130, Q131, Q132, Q133, Q134, Q135, Q136, Q137, Q138, Q139, Q140, Q141, Q142, Q143, Q144, Q145, Q146, Q147, Q148, Q149, Q150, Q151, Q152, Q153, Q154, Q155, Q156, Q157, Q158, Q159, Q160, Q161, Q162, Q163, Q164, Q165, Q166, Q167, Q168, Q169, Q170, Q171, Q172, Q173, Q174, Q175, Q176, Q177, Q178, Q179, Q180, Q181, Q182, Q183, Q184, Q185, Q186, Q187, Q188, Q189, Q190, Q191, Q192, Q193, Q194, Q195, Q196, Q197, Q198, Q199, Q200, Q201, Q202, Q203, Q204, Q205, Q206, Q207, Q208, Q209, Q210, Q211, Q212, Q213, Q214, Q215, Q216, Q217, Q218, Q219, Q220, Q221, Q222, Q223, Q224, Q225, Q226, Q227, Q228, Q229, Q230, Q231, Q232, Q233, Q234, Q235, Q236, Q237, Q238, Q239, Q240, Q241, Q242, Q243, Q244, Q245, Q246, Q247, Q248, Q249, Q250, Q251, Q252, Q253, Q254, Q255, Q256, Q257, Q258, Q259, Q260, Q261, Q262, Q263, Q264, Q265, Q266, Q267, Q268, Q269, Q270, Q271, Q272, Q273, Q274, Q275, Q276, Q277, Q278, Q279, Q280, Q281, Q282, Q283, Q284, Q285, Q286, Q287, Q288, Q289, Q290, Q291, Q292, Q293, Q294, Q295, Q296, Q297, Q298, Q299, Q300, Q301, Q302, Q303, Q304, Q305, Q306, Q307, Q308, Q309, Q310, Q311, Q312, Q313, Q314, Q315, Q316, Q317, Q318, Q319, Q320, Q321, Q322, Q323, Q324, Q325, Q326, Q327, Q328, Q329, Q330, Q331, Q332, Q333, Q334, Q335, Q336, Q337, Q338, Q339, Q340, Q341, Q342, Q343, Q344, Q345, Q346, Q347, Q348, Q349, Q350, Q351, Q352, Q353, Q354, Q355, Q356, Q357, Q358, Q359, Q360, Q361, Q362, Q363, Q364, Q365, Q366, Q367, Q368, Q369, Q370, Q371, Q372, Q373, Q374, Q375, Q376, Q377, Q378, Q379, Q380, Q381, Q382, Q383, Q384, Q385, Q386, Q387, Q388, Q389, Q390, Q391, Q392, Q393, Q394, Q395, Q396, Q397, Q398, Q399]), "targets" : qUnion([Q400])});
        }
    });
